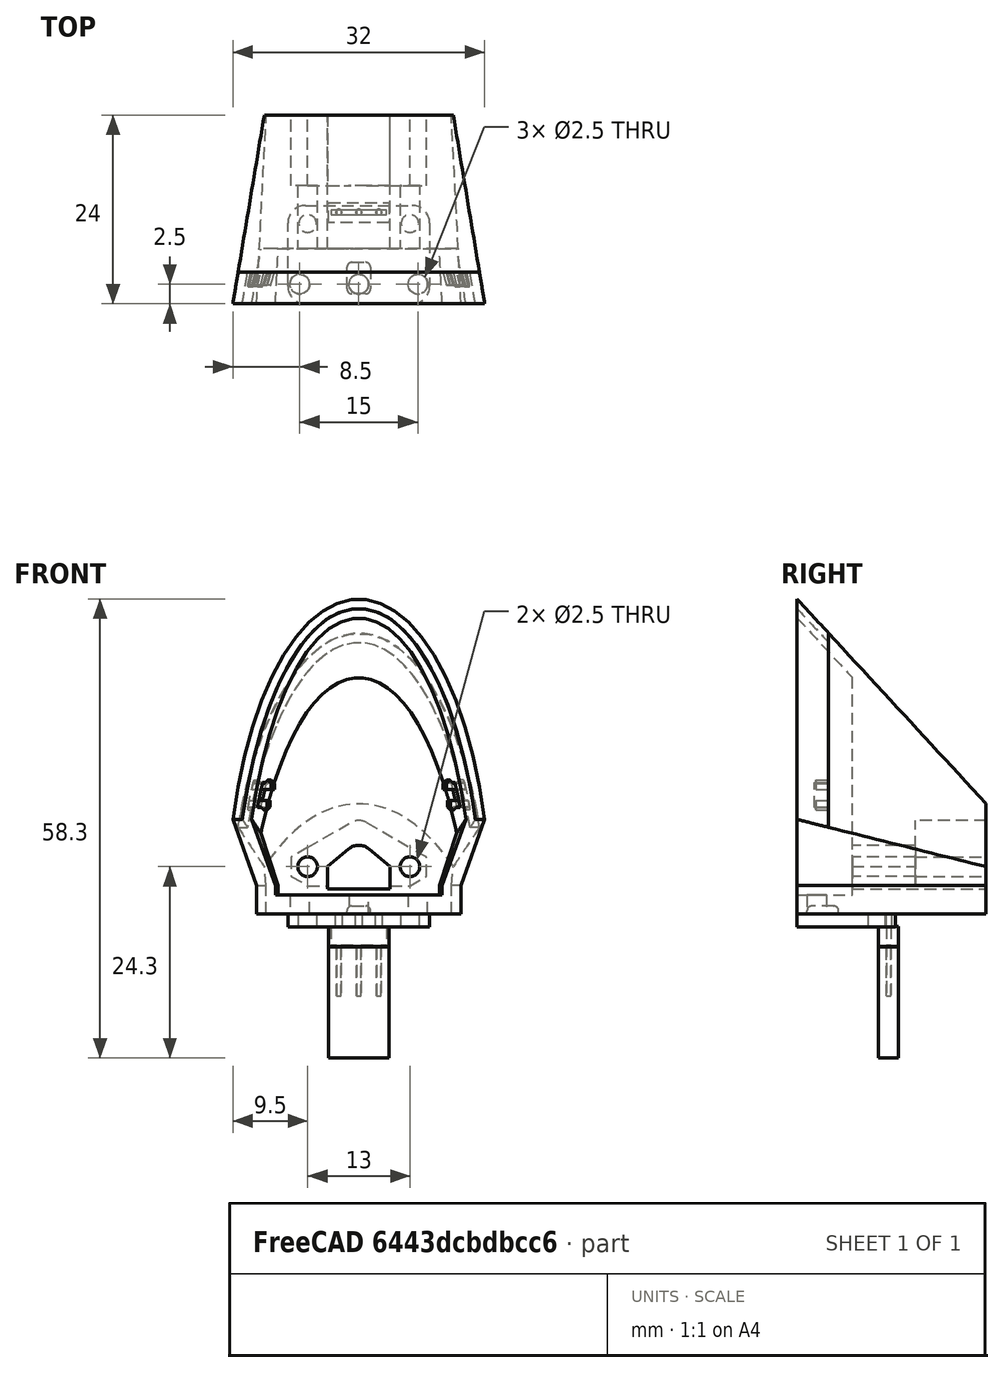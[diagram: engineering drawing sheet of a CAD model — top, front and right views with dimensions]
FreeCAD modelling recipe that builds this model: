
FCSTD DOCUMENT  (FreeCAD 0.19R24276 (Git))
Label: Spec_PB3D_Ear
License: All rights reserved
LicenseURL: http://en.wikipedia.org/wiki/All_rights_reserved
objects: Sketcher::SketchObject×30, PartDesign::Pocket×8, PartDesign::Pad×7, PartDesign::Body×7, PartDesign::Plane×5, PartDesign::SubtractiveLoft×4, Spreadsheet::Sheet×2, PartDesign::AdditiveLoft×2, App::Part×2, PartDesign::Fillet×1, Mesh::Feature×1
note: 86 computed .brp shape members not serialized (recipe doc carries the construction recipe); baked Part::Feature solids carry a one-line shape summary decoded from their .brp

FEATURE [PartDesign::Plane] DatumPlane  label="Datum_EarBack"
  AttachmentOffset = pos=(0,0,-24) rot=(0,0,1;0rad)
  Length = 61.2949
  MapMode = 5
  Placement = pos=(0,24,5.3e-15) rot=(1,0,0;1.5708rad)
  ResizeMode = 0
  Support = -> [XZ_Plane001]
  Width = 75.0828
  expr: .AttachmentOffset.Base.z = -<<params>>.ear_leng
FEATURE [Spreadsheet::Sheet] Spreadsheet  label="params"
  cells = A1=M2 Bolt Clearances; C1=M2.5 Bolt Clearances; E1=Std Dims; G1=Grove Board Dims; A2=Hole Clear Diam; B2(m2_hole_clear_diam)==2.5mm; C2=Hole Clear Diam; D2(m25_hole_clear_diam)==2.8mm; E2=Std. Chamfer; F2(std_chamf)==1mm; G2=Grove Board Width; H2(grove_board_width)==20mm; A3=Head Clear Diam; B3(m2_head_clear_diam)==4.2mm; C3=Head Clear Diam; D3(m25_head_clear_diam)==5.3mm; E3=Std. Radius; F3(std_rad)==2mm; G3=Grove Board Outer Mt Diam; H3(grove_board_mt_outer_diam)==4mm; A4=Head Min Depth; B4(m2_head_min_depth)==1.6mm; C4=Head Min Depth; D4(m25_head_min_depth)==2.3mm; E4=Std. Clear Tol; F4(std_clear_tol)==0.3mm; A5=Nut Clear Flat; B5(m2_nut_clear_flat)==4.2mm; C5=Nut Clear Flat; D5(m25_nut_clear_flat)==5.2mm; A6=Nut Min Depth; B6(m2_nut_min_depth)==1.75mm; C6=Nut Min Depth; D6(m25_nut_min_depth)==2mm; A8=Ear Dims; A9=Ear Base Thick; B9(ear_base_thick)==2mm; C9=Ear Leng; D9(ear_leng)==24mm; E9=Mic Mt Plane Offset Z; F9(mic_mt_plane_offset_z)==7mm; G9=Mic Pins Width; H9(mic_pins_width)==2.54mm * 3; A10=Ear Vert Height; B10(ear_vert_height)==1.6mm; C10=Ear Ellipse Maj Ax; D10(ear_ellipse_majax)==40mm; E10=Mic Mt Hex Offset; F10(mic_mt_hex_offset)==8mm; G10=Mic Pins Base Offset; H10(mic_pins_base_offset)==mic_mt_base_offset - 1.41mm; E11=Mic Mt Hole Space W; F11(mic_mt_hole_space_width)==13mm; G11=Mic Pins Square Block Dim; H11(mic_pins_square_block_dim)==2.54mm; A12=Ear Fr Base Width; B12(ear_front_base_width)==26mm; C12=Ear Mt Hole Offset; D12(ear_mt_hole_offset)==2.5mm; E12=Mic Mt Hole Base Offset; F12(mic_mt_base_offset)==ear_base_thick + 4mm; A13=Ear Fr Mid Width; B13(ear_front_mid_width)==32mm; C13=Ear Mt Hole Width Space; D13(ear_mt_hole_width)==15mm; A14=Ear Fr Mid Height; B14(ear_front_mid_height)==12mm; A15=Ear Fr Tot Height; B15(ear_front_tot_height)==40mm; C15=Ear Wall Thick; D15(ear_wall_thick)==2.4mm; G15=Ear Trm Leng; H15(ear_trim_leng)==4mm; G16=Ear Trm Thick; H16(ear_trim_thick)==1.2mm; A17=Ear Bk Base Width; B17(ear_back_base_width)==23.5mm; C17=Ear Sl Base Width; D17(ear_slope_base_width)==(ear_front_base_width - ear_back_base_width) / ear_leng; E17=Ear GM Base Width; F17(ear_gm_base_width)==ear_front_base_width - ear_slope_base_width * mic_mt_plane_offset_z; G17=Ear Trm Base Width; H17(ear_trim_base_width)==ear_front_base_width - ear_slope_base_width * ear_trim_leng; A18=Ear Bk Mid Width; B18(ear_back_mid_width)==24mm; C18=Ear Sl Mid Width; D18(ear_slope_mid_width)==(ear_front_mid_width - ear_back_mid_width) / ear_leng; E18=Ear GM Mid Width; F18(ear_gm_mid_width)==ear_front_mid_width - ear_slope_mid_width * mic_mt_plane_offset_z; G18=Ear Trm Mid Width; H18(ear_trim_mid_width)==ear_front_mid_width - ear_slope_mid_width * ear_trim_leng; A19=Ear Bk Mid Height; B19(ear_back_mid_height)==6mm; C19=Ear Sl Mid Height; D19(ear_slope_mid_height)==(ear_front_mid_height - ear_back_mid_height) / ear_leng; E19=Ear GM Mid Height; F19(ear_gm_mid_height)==ear_front_mid_height - ear_slope_mid_height * mic_mt_plane_offset_z; G19=Ear Trm Mid Height; H19(ear_trim_mid_height)==ear_front_mid_height - ear_slope_mid_height * ear_trim_leng; A20=Ear Bk Tot Height; B20(ear_back_tot_height)==14mm; C20=Ear Sl Tot Height; D20(ear_slope_tot_height)==(ear_front_tot_height - ear_back_tot_height) / ear_leng; E20=Ear GM Tot Height; F20(ear_gm_tot_height)==ear_front_tot_height - ear_slope_tot_height * mic_mt_plane_offset_z; G20=Ear Trm Tot Height; H20(ear_trim_tot_height)==ear_front_tot_height - ear_slope_tot_height * ear_trim_leng; G22=Ear Trm Clip Width; H22(ear_trim_clip_width)==1.6mm; G23=Ear Trm Clip Height; H23(ear_trim_clip_height)==3mm; G24=Ear Trm Clip Tol; H24(ear_trim_clip_tol)==0.2mm; G25=Ear Trm Clip Thick; H25(ear_trim_clip_thick)==0.8mm; G26=Ear Trm Clip Wedge Size; H26(ear_trim_clip_wedge_size)==0.4mm; G27=Ear Trm Clip Leng; H27(ear_trim_clip_leng)==ear_wall_thick - ear_trim_thick + ear_trim_clip_tol
FEATURE [Sketcher::SketchObject] Sketch  label="Sketch_EarFront"
  FullyConstrained = true
  MapMode = 5
  Placement = pos=(0,0,0) rot=(1,0,0;1.5708rad)
  Support = -> [XZ_Plane001]
  expr: Constraints[30] = <<params>>.ear_base_thick + <<params>>.ear_vert_height
  expr: Constraints[31] = <<params>>.ear_front_mid_height
  expr: Constraints[32] = <<params>>.ear_front_mid_width
  expr: Constraints[33] = <<params>>.ear_front_base_width
  expr: Constraints[34] = <<params>>.ear_front_tot_height
  expr: Constraints[35] = <<params>>.ear_ellipse_majax
  sketch-geometry (15):
    g0: LineSegment StartX=-13 StartY=0 StartZ=0 EndX=13 EndY=0 EndZ=0
    g1: LineSegment StartX=-13 StartY=0 StartZ=0 EndX=-13 EndY=3.6 EndZ=0
    g2: LineSegment StartX=13 StartY=0 StartZ=0 EndX=13 EndY=3.6 EndZ=0
    g3: LineSegment StartX=-13 StartY=3.6 StartZ=0 EndX=13 EndY=3.6 EndZ=0
    g4: LineSegment StartX=13 StartY=3.6 StartZ=0 EndX=16 EndY=12 EndZ=0
    g5: LineSegment StartX=-13 StartY=3.6 StartZ=0 EndX=-16 EndY=12 EndZ=0
    g6: ArcOfEllipse CenterX=0 CenterY=4e-16 CenterZ=0 NormalX=0 NormalY=0 NormalZ=1 MajorRadius=40 MinorRadius=16.7726 AngleXU=1.5708 StartAngle=5.01708 EndAngle=7.54929
    g7: LineSegment StartX=0 StartY=40 StartZ=0 EndX=0 EndY=-40 EndZ=0
    g8: LineSegment StartX=-16.7726 StartY=4e-16 StartZ=0 EndX=16.7726 EndY=4e-16 EndZ=0
    g9: GeomPoint X=4e-15 Y=36.3137 Z=0
    g10: GeomPoint X=0 Y=-36.3137 Z=0
    g11: LineSegment StartX=-16 StartY=12 StartZ=0 EndX=16 EndY=12 EndZ=0
    g12: LineSegment StartX=-13 StartY=3.6 StartZ=0 EndX=-13 EndY=12 EndZ=0
    g13: LineSegment StartX=13 StartY=3.6 StartZ=0 EndX=13 EndY=12 EndZ=0
    g14: LineSegment StartX=-16 StartY=12 StartZ=0 EndX=16 EndY=12 EndZ=0
  constraints (33):
    c: Horizontal(g0)
    c: Symmetric(g0,g0,g-1)
    c: Coincident(g1,g0)
    c: Vertical(g1)
    c: Coincident(g2,g0)
    c: Vertical(g2)
    c: Coincident(g3,g1)
    c: Coincident(g3,g2)
    c: Horizontal(g3)
    c: Coincident(g4,g2)
    c: Coincident(g5,g1)
    c: InternalAlignment(g7-g10 -> g6) x4
    c: PointOnObject(g6,g-2)
    c: Coincident(g11,g5)
    c: Coincident(g11,g4)
    c: Horizontal(g11)
    c: Coincident(g12,g1)
    c: PointOnObject(g12,g11)
    c: Vertical(g12)
    c: Coincident(g13,g2)
    c: PointOnObject(g13,g11)
    c: Vertical(g13)
    c: PointOnObject(g7,g-2)
    c: Coincident(g14,g6)
    c: Coincident(g14,g6)
    c: Coincident(g6,g5)
    c: Coincident(g6,g4)
    c: DistanceY(g0,g2) = 3.6
    c: DistanceY(g-1,g4) = 12
    c: DistanceX(g5,g4) = 32
    c: DistanceX(g0,g0) = 26
    c: DistanceY(g-1,g7) = 40
    c: DistanceY(g8,g7) = 40
FEATURE [Sketcher::SketchObject] Sketch001  label="Sketch_EarBack"
  FullyConstrained = true
  MapMode = 5
  Placement = pos=(0,24,5.3e-15) rot=(1,0,0;1.5708rad)
  Support = -> [DatumPlane]
  expr: Constraints[33] = <<params>>.ear_back_base_width
  expr: Constraints[32] = <<params>>.ear_back_mid_width
  expr: Constraints[31] = <<params>>.ear_back_mid_height
  expr: Constraints[30] = <<params>>.ear_base_thick + <<params>>.ear_vert_height
  expr: Constraints[34] = <<params>>.ear_back_tot_height
  expr: Constraints[35] = <<params>>.ear_ellipse_majax
  sketch-geometry (15):
    g0: LineSegment StartX=-11.75 StartY=0 StartZ=0 EndX=11.75 EndY=0 EndZ=0
    g1: LineSegment StartX=-11.75 StartY=0 StartZ=0 EndX=-11.75 EndY=3.6 EndZ=0
    g2: LineSegment StartX=11.75 StartY=0 StartZ=0 EndX=11.75 EndY=3.6 EndZ=0
    g3: LineSegment StartX=-11.75 StartY=3.6 StartZ=0 EndX=11.75 EndY=3.6 EndZ=0
    g4: LineSegment StartX=11.75 StartY=3.6 StartZ=0 EndX=12 EndY=6 EndZ=0
    g5: LineSegment StartX=-11.75 StartY=3.6 StartZ=0 EndX=-12 EndY=6 EndZ=0
    g6: ArcOfEllipse CenterX=0 CenterY=-26 CenterZ=0 NormalX=0 NormalY=0 NormalZ=1 MajorRadius=40 MinorRadius=20 AngleXU=1.5708 StartAngle=5.63968 EndAngle=6.92669
    g7: LineSegment StartX=0 StartY=14 StartZ=0 EndX=0 EndY=-66 EndZ=0
    g8: LineSegment StartX=-20 StartY=-26 StartZ=0 EndX=20 EndY=-26 EndZ=0
    g9: GeomPoint X=3.8e-15 Y=8.64102 Z=0
    g10: GeomPoint X=0 Y=-60.641 Z=0
    g11: LineSegment StartX=-12 StartY=6 StartZ=0 EndX=12 EndY=6 EndZ=0
    g12: LineSegment StartX=-11.75 StartY=3.6 StartZ=0 EndX=-11.75 EndY=6 EndZ=0
    g13: LineSegment StartX=11.75 StartY=3.6 StartZ=0 EndX=11.75 EndY=6 EndZ=0
    g14: LineSegment StartX=-12 StartY=6 StartZ=0 EndX=12 EndY=6 EndZ=0
  constraints (33):
    c: Horizontal(g0)
    c: Symmetric(g0,g0,g-1)
    c: Coincident(g1,g0)
    c: Vertical(g1)
    c: Coincident(g2,g0)
    c: Vertical(g2)
    c: Coincident(g3,g1)
    c: Coincident(g3,g2)
    c: Horizontal(g3)
    c: Coincident(g4,g2)
    c: Coincident(g5,g1)
    c: InternalAlignment(g7-g10 -> g6) x4
    c: PointOnObject(g6,g-2)
    c: Coincident(g11,g5)
    c: Coincident(g11,g4)
    c: Horizontal(g11)
    c: Coincident(g12,g1)
    c: PointOnObject(g12,g11)
    c: Vertical(g12)
    c: Coincident(g13,g2)
    c: PointOnObject(g13,g11)
    c: Vertical(g13)
    c: PointOnObject(g7,g-2)
    c: Coincident(g14,g6)
    c: Coincident(g14,g6)
    c: Coincident(g6,g5)
    c: Coincident(g6,g4)
    c: DistanceY(g0,g2) = 3.6
    c: DistanceY(g-1,g4) = 6
    c: DistanceX(g5,g4) = 24
    c: DistanceX(g0,g0) = 23.5
    c: DistanceY(g-1,g7) = 14
    c: DistanceY(g6,g7) = 40
FEATURE [PartDesign::AdditiveLoft] AdditiveLoft  label="AdditiveLoft_MainEar"
  Closed = false
  Placement = pos=(0,0,0) rot=(1,0,0;1.5708rad)
  Profile = -> Sketch
  Ruled = false
  Sections = -> [Sketch001]
FEATURE [Sketcher::SketchObject] Sketch002
  FullyConstrained = true
  MapMode = 5
  Support = -> [XY_Plane001]
  expr: Constraints[7] = <<params>>.ear_mt_hole_width
  expr: Constraints[8] = <<params>>.ear_mt_hole_offset
  expr: Constraints[9] = <<params>>.m2_hole_clear_diam
  sketch-geometry (5):
    g0: LineSegment StartX=-7.5 StartY=2.5 StartZ=0 EndX=7.5 EndY=2.5 EndZ=0
    g1: GeomPoint X=0 Y=2.5 Z=0
    g2: Circle CenterX=0 CenterY=2.5 CenterZ=0 NormalX=0 NormalY=0 NormalZ=1 AngleXU=0 Radius=1.25
    g3: Circle CenterX=7.5 CenterY=2.5 CenterZ=0 NormalX=0 NormalY=0 NormalZ=1 AngleXU=0 Radius=1.25
    g4: Circle CenterX=-7.5 CenterY=2.5 CenterZ=0 NormalX=0 NormalY=0 NormalZ=1 AngleXU=0 Radius=1.25
  constraints (11):
    c: Horizontal(g0)
    c: PointOnObject(g1,g-2)
    c: Symmetric(g0,g0,g1)
    c: Coincident(g2,g1)
    c: Coincident(g3,g0)
    c: Coincident(g4,g0)
    c: Equal(g2,g3)
    c: DistanceX(g4,g3) = 15
    c: DistanceY(g-1,g2) = 2.5
    c: Diameter(g3) = 2.5
    c: Equal(g2,g4)
FEATURE [PartDesign::Pocket] Pocket  label="Pocket_MtHoles"
  BaseFeature = -> AdditiveLoft
  Length = 6
  Length2 = 100
  Placement = pos=(0,0,0) rot=(1,0,0;1.5708rad)
  Profile = -> Sketch002
  Reversed = true
  Type = 0
  expr: Length = <<params>>.ear_base_thick * 3
FEATURE [Sketcher::SketchObject] Sketch003  label="Sketch_EarFr_Temp"
  FullyConstrained = true
  MapMode = 5
  Placement = pos=(0,0,0) rot=(1,0,0;1.5708rad)
  Support = -> [XZ_Plane001]
  expr: Constraints[35] = <<params>>.ear_ellipse_majax
  expr: Constraints[34] = <<params>>.ear_front_tot_height
  expr: Constraints[33] = <<params>>.ear_front_base_width
  expr: Constraints[32] = <<params>>.ear_front_mid_width
  expr: Constraints[31] = <<params>>.ear_front_mid_height
  expr: Constraints[30] = <<params>>.ear_base_thick + <<params>>.ear_vert_height
  sketch-geometry (15):
    g0: LineSegment StartX=-13 StartY=0 StartZ=0 EndX=13 EndY=0 EndZ=0
    g1: LineSegment StartX=-13 StartY=0 StartZ=0 EndX=-13 EndY=3.6 EndZ=0
    g2: LineSegment StartX=13 StartY=0 StartZ=0 EndX=13 EndY=3.6 EndZ=0
    g3: LineSegment StartX=-13 StartY=3.6 StartZ=0 EndX=13 EndY=3.6 EndZ=0
    g4: LineSegment StartX=13 StartY=3.6 StartZ=0 EndX=16 EndY=12 EndZ=0
    g5: LineSegment StartX=-13 StartY=3.6 StartZ=0 EndX=-16 EndY=12 EndZ=0
    g6: ArcOfEllipse CenterX=0 CenterY=-7e-16 CenterZ=0 NormalX=0 NormalY=0 NormalZ=1 MajorRadius=40 MinorRadius=16.7726 AngleXU=1.5708 StartAngle=5.01708 EndAngle=7.54929
    g7: LineSegment StartX=0 StartY=40 StartZ=0 EndX=0 EndY=-40 EndZ=0
    g8: LineSegment StartX=-16.7726 StartY=-7e-16 StartZ=0 EndX=16.7726 EndY=-7e-16 EndZ=0
    g9: GeomPoint X=4e-15 Y=36.3137 Z=0
    g10: GeomPoint X=0 Y=-36.3137 Z=0
    g11: LineSegment StartX=-16 StartY=12 StartZ=0 EndX=16 EndY=12 EndZ=0
    g12: LineSegment StartX=-13 StartY=3.6 StartZ=0 EndX=-13 EndY=12 EndZ=0
    g13: LineSegment StartX=13 StartY=3.6 StartZ=0 EndX=13 EndY=12 EndZ=0
    g14: LineSegment StartX=-16 StartY=12 StartZ=0 EndX=16 EndY=12 EndZ=0
  constraints (33):
    c: Horizontal(g0)
    c: Symmetric(g0,g0,g-1)
    c: Coincident(g1,g0)
    c: Vertical(g1)
    c: Coincident(g2,g0)
    c: Vertical(g2)
    c: Coincident(g3,g1)
    c: Coincident(g3,g2)
    c: Horizontal(g3)
    c: Coincident(g4,g2)
    c: Coincident(g5,g1)
    c: InternalAlignment(g7-g10 -> g6) x4
    c: PointOnObject(g6,g-2)
    c: Coincident(g11,g5)
    c: Coincident(g11,g4)
    c: Horizontal(g11)
    c: Coincident(g12,g1)
    c: PointOnObject(g12,g11)
    c: Vertical(g12)
    c: Coincident(g13,g2)
    c: PointOnObject(g13,g11)
    c: Vertical(g13)
    c: PointOnObject(g7,g-2)
    c: Coincident(g14,g6)
    c: Coincident(g14,g6)
    c: Coincident(g6,g5)
    c: Coincident(g6,g4)
    c: DistanceY(g0,g2) = 3.6
    c: DistanceY(g-1,g4) = 12
    c: DistanceX(g5,g4) = 32
    c: DistanceX(g0,g0) = 26
    c: DistanceY(g-1,g7) = 40
    c: DistanceY(g8,g7) = 40
FEATURE [Sketcher::SketchObject] Sketch004  label="Sketch_EarBk_Temp"
  FullyConstrained = true
  MapMode = 5
  Placement = pos=(0,24,5.3e-15) rot=(1,0,0;1.5708rad)
  Support = -> [DatumPlane]
  expr: Constraints[35] = <<params>>.ear_ellipse_majax
  expr: Constraints[34] = <<params>>.ear_back_tot_height
  expr: Constraints[30] = <<params>>.ear_base_thick + <<params>>.ear_vert_height
  expr: Constraints[31] = <<params>>.ear_back_mid_height
  expr: Constraints[32] = <<params>>.ear_back_mid_width
  expr: Constraints[33] = <<params>>.ear_back_base_width
  sketch-geometry (15):
    g0: LineSegment StartX=-11.75 StartY=0 StartZ=0 EndX=11.75 EndY=0 EndZ=0
    g1: LineSegment StartX=-11.75 StartY=0 StartZ=0 EndX=-11.75 EndY=3.6 EndZ=0
    g2: LineSegment StartX=11.75 StartY=0 StartZ=0 EndX=11.75 EndY=3.6 EndZ=0
    g3: LineSegment StartX=-11.75 StartY=3.6 StartZ=0 EndX=11.75 EndY=3.6 EndZ=0
    g4: LineSegment StartX=11.75 StartY=3.6 StartZ=0 EndX=12 EndY=6 EndZ=0
    g5: LineSegment StartX=-11.75 StartY=3.6 StartZ=0 EndX=-12 EndY=6 EndZ=0
    g6: ArcOfEllipse CenterX=0 CenterY=-26 CenterZ=0 NormalX=0 NormalY=0 NormalZ=1 MajorRadius=40 MinorRadius=20 AngleXU=1.5708 StartAngle=5.63968 EndAngle=6.92669
    g7: LineSegment StartX=0 StartY=14 StartZ=0 EndX=0 EndY=-66 EndZ=0
    g8: LineSegment StartX=-20 StartY=-26 StartZ=0 EndX=20 EndY=-26 EndZ=0
    g9: GeomPoint X=3.8e-15 Y=8.64102 Z=0
    g10: GeomPoint X=0 Y=-60.641 Z=0
    g11: LineSegment StartX=-12 StartY=6 StartZ=0 EndX=12 EndY=6 EndZ=0
    g12: LineSegment StartX=-11.75 StartY=3.6 StartZ=0 EndX=-11.75 EndY=6 EndZ=0
    g13: LineSegment StartX=11.75 StartY=3.6 StartZ=0 EndX=11.75 EndY=6 EndZ=0
    g14: LineSegment StartX=-12 StartY=6 StartZ=0 EndX=12 EndY=6 EndZ=0
  constraints (33):
    c: Horizontal(g0)
    c: Symmetric(g0,g0,g-1)
    c: Coincident(g1,g0)
    c: Vertical(g1)
    c: Coincident(g2,g0)
    c: Vertical(g2)
    c: Coincident(g3,g1)
    c: Coincident(g3,g2)
    c: Horizontal(g3)
    c: Coincident(g4,g2)
    c: Coincident(g5,g1)
    c: InternalAlignment(g7-g10 -> g6) x4
    c: PointOnObject(g6,g-2)
    c: Coincident(g11,g5)
    c: Coincident(g11,g4)
    c: Horizontal(g11)
    c: Coincident(g12,g1)
    c: PointOnObject(g12,g11)
    c: Vertical(g12)
    c: Coincident(g13,g2)
    c: PointOnObject(g13,g11)
    c: Vertical(g13)
    c: PointOnObject(g7,g-2)
    c: Coincident(g14,g6)
    c: Coincident(g14,g6)
    c: Coincident(g6,g5)
    c: Coincident(g6,g4)
    c: DistanceY(g0,g2) = 3.6
    c: DistanceY(g-1,g4) = 6
    c: DistanceX(g5,g4) = 24
    c: DistanceX(g0,g0) = 23.5
    c: DistanceY(g-1,g7) = 14
    c: DistanceY(g6,g7) = 40
FEATURE [PartDesign::Plane] DatumPlane001  label="Datum_MicMtPlane"
  AttachmentOffset = pos=(0,0,-7) rot=(0,0,1;0rad)
  Length = 61.2949
  MapMode = 5
  Placement = pos=(0,7,1.6e-15) rot=(1,0,0;1.5708rad)
  ResizeMode = 0
  Support = -> [XZ_Plane001]
  Width = 75.0828
  expr: .AttachmentOffset.Base.z = -<<params>>.mic_mt_plane_offset_z
FEATURE [Sketcher::SketchObject] Sketch015  label="Sketch_GrovePCut"
  FullyConstrained = true
  MapMode = 5
  Placement = pos=(0,7,1.6e-15) rot=(1,0,0;1.5708rad)
  Support = -> [DatumPlane001]
  expr: Constraints[30] = <<params>>.grove_board_width + <<params>>.std_clear_tol
  expr: Constraints[32] = <<params>>.grove_board_mt_outer_diam + <<params>>.std_clear_tol
  expr: Constraints[29] = <<params>>.grove_board_width + <<params>>.std_clear_tol
  expr: Constraints[4] = <<params>>.ear_base_thick - <<params>>.std_clear_tol / 2
  sketch-geometry (12):
    g0: LineSegment StartX=-10.15 StartY=22.15 StartZ=0 EndX=10.15 EndY=22.15 EndZ=0
    g1: LineSegment StartX=10.15 StartY=1.85 StartZ=0 EndX=-10.15 EndY=1.85 EndZ=0
    g2: GeomPoint X=0 Y=1.85 Z=0
    g3: LineSegment StartX=-10.15 StartY=22.15 StartZ=0 EndX=-10.15 EndY=14.15 EndZ=0
    g4: LineSegment StartX=-10.15 StartY=1.85 StartZ=0 EndX=-10.15 EndY=9.85 EndZ=0
    g5: LineSegment StartX=10.15 StartY=1.85 StartZ=0 EndX=10.15 EndY=9.85 EndZ=0
    g6: LineSegment StartX=10.15 StartY=22.15 StartZ=0 EndX=10.15 EndY=14.15 EndZ=0
    g7: ArcOfCircle CenterX=-10.15 CenterY=12 CenterZ=0 NormalX=0 NormalY=0 NormalZ=1 AngleXU=0 Radius=2.15 StartAngle=1.5708 EndAngle=4.71239
    g8: ArcOfCircle CenterX=10.15 CenterY=12 CenterZ=0 NormalX=0 NormalY=0 NormalZ=1 AngleXU=0 Radius=2.15 StartAngle=4.71239 EndAngle=7.85398
    g9: LineSegment StartX=-10.15 StartY=14.15 StartZ=0 EndX=-10.15 EndY=9.85 EndZ=0
    g10: LineSegment StartX=10.15 StartY=14.15 StartZ=0 EndX=10.15 EndY=9.85 EndZ=0
    g11: LineSegment StartX=-10.15 StartY=12 StartZ=0 EndX=10.15 EndY=12 EndZ=0
  constraints (33):
    c: Horizontal(g0)
    c: Horizontal(g1)
    c: PointOnObject(g2,g-2)
    c: Symmetric(g1,g1,g2)
    c: DistanceY(g-1,g2) = 1.85
    c: Coincident(g3,g0)
    c: Vertical(g3)
    c: Coincident(g4,g1)
    c: Vertical(g4)
    c: Coincident(g5,g1)
    c: Vertical(g5)
    c: Coincident(g6,g0)
    c: Vertical(g6)
    c: Coincident(g7,g3)
    c: Coincident(g7,g4)
    c: Coincident(g8,g6)
    c: Coincident(g8,g5)
    c: Coincident(g9,g3)
    c: Coincident(g9,g4)
    c: Vertical(g9)
    c: Coincident(g10,g6)
    c: Coincident(g10,g5)
    c: Vertical(g10)
    c: PointOnObject(g7,g9)
    c: PointOnObject(g8,g10)
    c: Coincident(g11,g7)
    c: Coincident(g11,g8)
    c: Horizontal(g11)
    c: Equal(g6,g5)
    c: DistanceY(g1,g0) = 20.3
    c: DistanceX(g0,g0) = 20.3
    c: Equal(g8,g7)
    c: Diameter(g8) = 4.3
FEATURE [Sketcher::SketchObject] Sketch016  label="Sketch_EarFront_Cut"
  FullyConstrained = true
  MapMode = 5
  Placement = pos=(0,0,0) rot=(1,0,0;1.5708rad)
  Support = -> [XZ_Plane001]
  expr: Constraints[61] = <<params>>.ear_ellipse_majax
  expr: Constraints[52] = <<params>>.ear_wall_thick
  expr: Constraints[60] = <<params>>.ear_wall_thick
  expr: Constraints[35] = <<params>>.ear_ellipse_majax
  expr: Constraints[50] = Spreadsheet.ear_wall_thick
  expr: Constraints[34] = <<params>>.ear_front_tot_height
  expr: Constraints[49] = Spreadsheet.ear_wall_thick
  expr: Constraints[33] = <<params>>.ear_front_base_width
  expr: Constraints[32] = <<params>>.ear_front_mid_width
  expr: Constraints[51] = <<params>>.ear_wall_thick
  expr: Constraints[31] = <<params>>.ear_front_mid_height
  expr: Constraints[30] = <<params>>.ear_base_thick + <<params>>.ear_vert_height
  sketch-geometry (26):
    g0: LineSegment StartX=-13 StartY=0 StartZ=0 EndX=13 EndY=0 EndZ=0
    g1: LineSegment StartX=-13 StartY=0 StartZ=0 EndX=-13 EndY=3.6 EndZ=0
    g2: LineSegment StartX=13 StartY=0 StartZ=0 EndX=13 EndY=3.6 EndZ=0
    g3: LineSegment StartX=-13 StartY=3.6 StartZ=0 EndX=13 EndY=3.6 EndZ=0
    g4: LineSegment StartX=13 StartY=3.6 StartZ=0 EndX=16 EndY=12 EndZ=0
    g5: LineSegment StartX=-13 StartY=3.6 StartZ=0 EndX=-16 EndY=12 EndZ=0
    g6: ArcOfEllipse CenterX=0 CenterY=7e-16 CenterZ=0 NormalX=0 NormalY=0 NormalZ=1 MajorRadius=40 MinorRadius=16.7726 AngleXU=1.5708 StartAngle=5.01708 EndAngle=7.54929
    g7: LineSegment StartX=0 StartY=40 StartZ=0 EndX=0 EndY=-40 EndZ=0
    g8: LineSegment StartX=-16.7726 StartY=7e-16 StartZ=0 EndX=16.7726 EndY=7e-16 EndZ=0
    g9: GeomPoint X=4e-15 Y=36.3137 Z=0
    g10: GeomPoint X=0 Y=-36.3137 Z=0
    g11: LineSegment StartX=-16 StartY=12 StartZ=0 EndX=16 EndY=12 EndZ=0
    g12: LineSegment StartX=-13 StartY=3.6 StartZ=0 EndX=-13 EndY=12 EndZ=0
    g13: LineSegment StartX=13 StartY=3.6 StartZ=0 EndX=13 EndY=12 EndZ=0
    g14: LineSegment StartX=-16 StartY=12 StartZ=0 EndX=16 EndY=12 EndZ=0
    g15: LineSegment StartX=-10.6 StartY=2.4 StartZ=0 EndX=10.6 EndY=2.4 EndZ=0
    g16: GeomPoint X=0 Y=2.4 Z=0
    g17: LineSegment StartX=-10.6 StartY=2.4 StartZ=0 EndX=-10.6 EndY=3.6 EndZ=0
    g18: LineSegment StartX=-10.6 StartY=3.6 StartZ=0 EndX=-13.6 EndY=12 EndZ=0
    g19: LineSegment StartX=10.6 StartY=2.4 StartZ=0 EndX=10.6 EndY=3.6 EndZ=0
    g20: LineSegment StartX=10.6 StartY=3.6 StartZ=0 EndX=13.6 EndY=12 EndZ=0
    g21: ArcOfEllipse CenterX=0 CenterY=-2.4 CenterZ=0 NormalX=0 NormalY=0 NormalZ=1 MajorRadius=40 MinorRadius=14.5774 AngleXU=1.5708 StartAngle=5.08066 EndAngle=7.48571
    g22: LineSegment StartX=-7e-16 StartY=37.6 StartZ=0 EndX=7e-16 EndY=-42.4 EndZ=0
    g23: LineSegment StartX=-14.5774 StartY=-2.4 StartZ=0 EndX=14.5774 EndY=-2.4 EndZ=0
    g24: GeomPoint X=4.1e-15 Y=34.8492 Z=0
    g25: GeomPoint X=6e-16 Y=-39.6492 Z=0
  constraints (56):
    c: Horizontal(g0)
    c: Symmetric(g0,g0,g-1)
    c: Coincident(g1,g0)
    c: Vertical(g1)
    c: Coincident(g2,g0)
    c: Vertical(g2)
    c: Coincident(g3,g1)
    c: Coincident(g3,g2)
    c: Horizontal(g3)
    c: Coincident(g4,g2)
    c: Coincident(g5,g1)
    c: InternalAlignment(g7-g10 -> g6) x4
    c: PointOnObject(g6,g-2)
    c: Coincident(g11,g5)
    c: Coincident(g11,g4)
    c: Horizontal(g11)
    c: Coincident(g12,g1)
    c: PointOnObject(g12,g11)
    c: Vertical(g12)
    c: Coincident(g13,g2)
    c: PointOnObject(g13,g11)
    c: Vertical(g13)
    c: PointOnObject(g7,g-2)
    c: Coincident(g14,g6)
    c: Coincident(g14,g6)
    c: Coincident(g6,g5)
    c: Coincident(g6,g4)
    c: DistanceY(g0,g2) = 3.6
    c: DistanceY(g-1,g4) = 12
    c: DistanceX(g5,g4) = 32
    c: DistanceX(g0,g0) = 26
    c: DistanceY(g-1,g7) = 40
    c: DistanceY(g8,g7) = 40
    c: Horizontal(g15)
    c: PointOnObject(g16,g7)
    c: Symmetric(g15,g15,g16)
    c: Coincident(g17,g15)
    c: PointOnObject(g17,g3)
    c: Vertical(g17)
    c: Coincident(g18,g17)
    c: PointOnObject(g18,g11)
    c: Coincident(g19,g15)
    c: PointOnObject(g19,g3)
    c: Vertical(g19)
    c: Coincident(g20,g19)
    c: PointOnObject(g20,g11)
    c: DistanceX(g19,g2) = 2.4
    c: DistanceY(g-1,g16) = 2.4
    c: DistanceX(g20,g4) = 2.4
    c: DistanceX(g5,g18) = 2.4
    c: InternalAlignment(g22-g25 -> g21) x4
    c: PointOnObject(g21,g7)
    c: Coincident(g21,g18)
    c: Coincident(g21,g20)
    c: DistanceY(g22,g7) = 2.4
    c: DistanceY(g21,g22) = 40
FEATURE [Sketcher::SketchObject] Sketch017  label="Sketch_EarMicMt_Cut"
  FullyConstrained = true
  MapMode = 5
  Placement = pos=(0,7,1.6e-15) rot=(1,0,0;1.5708rad)
  Support = -> [DatumPlane001]
  expr: Constraints[30] = <<params>>.ear_base_thick + <<params>>.ear_vert_height
  expr: Constraints[31] = <<params>>.ear_gm_mid_height
  expr: Constraints[51] = <<params>>.ear_wall_thick
  expr: Constraints[32] = <<params>>.ear_gm_mid_width
  expr: Constraints[33] = <<params>>.ear_gm_base_width
  expr: Constraints[49] = Spreadsheet.ear_wall_thick
  expr: Constraints[34] = <<params>>.ear_gm_tot_height
  expr: Constraints[50] = Spreadsheet.ear_wall_thick
  expr: Constraints[35] = <<params>>.ear_ellipse_majax
  expr: Constraints[60] = <<params>>.ear_wall_thick
  expr: Constraints[52] = <<params>>.ear_wall_thick
  expr: Constraints[61] = <<params>>.ear_ellipse_majax
  sketch-geometry (26):
    g0: LineSegment StartX=-12.6354 StartY=0 StartZ=0 EndX=12.6354 EndY=0 EndZ=0
    g1: LineSegment StartX=-12.6354 StartY=0 StartZ=0 EndX=-12.6354 EndY=3.6 EndZ=0
    g2: LineSegment StartX=12.6354 StartY=0 StartZ=0 EndX=12.6354 EndY=3.6 EndZ=0
    g3: LineSegment StartX=-12.6354 StartY=3.6 StartZ=0 EndX=12.6354 EndY=3.6 EndZ=0
    g4: LineSegment StartX=12.6354 StartY=3.6 StartZ=0 EndX=14.8333 EndY=10.25 EndZ=0
    g5: LineSegment StartX=-12.6354 StartY=3.6 StartZ=0 EndX=-14.8333 EndY=10.25 EndZ=0
    g6: ArcOfEllipse CenterX=0 CenterY=-7.58333 CenterZ=0 NormalX=0 NormalY=0 NormalZ=1 MajorRadius=40 MinorRadius=16.5714 AngleXU=1.5708 StartAngle=5.17449 EndAngle=7.39188
    g7: LineSegment StartX=0 StartY=32.4167 StartZ=0 EndX=0 EndY=-47.5833 EndZ=0
    g8: LineSegment StartX=-16.5714 StartY=-7.58333 StartZ=0 EndX=16.5714 EndY=-7.58333 EndZ=0
    g9: GeomPoint X=4e-15 Y=28.8226 Z=0
    g10: GeomPoint X=0 Y=-43.9892 Z=0
    g11: LineSegment StartX=-14.8333 StartY=10.25 StartZ=0 EndX=14.8333 EndY=10.25 EndZ=0
    g12: LineSegment StartX=-12.6354 StartY=3.6 StartZ=0 EndX=-12.6354 EndY=10.25 EndZ=0
    g13: LineSegment StartX=12.6354 StartY=3.6 StartZ=0 EndX=12.6354 EndY=10.25 EndZ=0
    g14: LineSegment StartX=-14.8333 StartY=10.25 StartZ=0 EndX=14.8333 EndY=10.25 EndZ=0
    g15: LineSegment StartX=-10.2354 StartY=2.4 StartZ=0 EndX=10.2354 EndY=2.4 EndZ=0
    g16: GeomPoint X=0 Y=2.4 Z=0
    g17: LineSegment StartX=-10.2354 StartY=2.4 StartZ=0 EndX=-10.2354 EndY=3.6 EndZ=0
    g18: LineSegment StartX=-10.2354 StartY=3.6 StartZ=0 EndX=-12.4333 EndY=10.25 EndZ=0
    g19: LineSegment StartX=10.2354 StartY=2.4 StartZ=0 EndX=10.2354 EndY=3.6 EndZ=0
    g20: LineSegment StartX=10.2354 StartY=3.6 StartZ=0 EndX=12.4333 EndY=10.25 EndZ=0
    g21: ArcOfEllipse CenterX=0 CenterY=-9.98333 CenterZ=0 NormalX=0 NormalY=0 NormalZ=1 MajorRadius=40 MinorRadius=14.4133 AngleXU=1.5708 StartAngle=5.24274 EndAngle=7.32363
    g22: LineSegment StartX=-2.9e-15 StartY=30.0167 StartZ=0 EndX=2.9e-15 EndY=-49.9833 EndZ=0
    g23: LineSegment StartX=-14.4133 StartY=-9.98333 StartZ=0 EndX=14.4133 EndY=-9.98333 EndZ=0
    g24: GeomPoint X=-8.3e-15 Y=27.3296 Z=0
    g25: GeomPoint X=2.8e-15 Y=-47.2963 Z=0
  constraints (56):
    c: Horizontal(g0)
    c: Symmetric(g0,g0,g-1)
    c: Coincident(g1,g0)
    c: Vertical(g1)
    c: Coincident(g2,g0)
    c: Vertical(g2)
    c: Coincident(g3,g1)
    c: Coincident(g3,g2)
    c: Horizontal(g3)
    c: Coincident(g4,g2)
    c: Coincident(g5,g1)
    c: InternalAlignment(g7-g10 -> g6) x4
    c: PointOnObject(g6,g-2)
    c: Coincident(g11,g5)
    c: Coincident(g11,g4)
    c: Horizontal(g11)
    c: Coincident(g12,g1)
    c: PointOnObject(g12,g11)
    c: Vertical(g12)
    c: Coincident(g13,g2)
    c: PointOnObject(g13,g11)
    c: Vertical(g13)
    c: PointOnObject(g7,g-2)
    c: Coincident(g14,g6)
    c: Coincident(g14,g6)
    c: Coincident(g6,g5)
    c: Coincident(g6,g4)
    c: DistanceY(g0,g2) = 3.6
    c: DistanceY(g-1,g4) = 10.25
    c: DistanceX(g5,g4) = 29.6667
    c: DistanceX(g0,g0) = 25.2708
    c: DistanceY(g-1,g7) = 32.4167
    c: DistanceY(g8,g7) = 40
    c: Horizontal(g15)
    c: PointOnObject(g16,g7)
    c: Symmetric(g15,g15,g16)
    c: Coincident(g17,g15)
    c: PointOnObject(g17,g3)
    c: Vertical(g17)
    c: Coincident(g18,g17)
    c: PointOnObject(g18,g11)
    c: Coincident(g19,g15)
    c: PointOnObject(g19,g3)
    c: Vertical(g19)
    c: Coincident(g20,g19)
    c: PointOnObject(g20,g11)
    c: DistanceX(g19,g2) = 2.4
    c: DistanceY(g-1,g16) = 2.4
    c: DistanceX(g20,g4) = 2.4
    c: DistanceX(g5,g18) = 2.4
    c: InternalAlignment(g22-g25 -> g21) x4
    c: PointOnObject(g21,g7)
    c: Coincident(g21,g18)
    c: Coincident(g21,g20)
    c: DistanceY(g22,g7) = 2.4
    c: DistanceY(g21,g22) = 40
FEATURE [PartDesign::SubtractiveLoft] SubtractiveLoft
  BaseFeature = -> Pocket
  Closed = false
  Placement = pos=(0,0,0) rot=(1,0,0;1.5708rad)
  Profile = -> Sketch016
  Ruled = false
  Sections = -> [Sketch017]
FEATURE [Sketcher::SketchObject] Sketch018
  FullyConstrained = true
  MapMode = 5
  Placement = pos=(0,7,1.6e-15) rot=(1,0,0;1.5708rad)
  Support = -> [DatumPlane001]
  expr: Constraints[8] = <<params>>.mic_mt_base_offset
  expr: Constraints[7] = <<params>>.m2_hole_clear_diam
  expr: Constraints[3] = <<params>>.mic_mt_hole_space_width
  sketch-geometry (4):
    g0: LineSegment StartX=-6.5 StartY=6 StartZ=0 EndX=6.5 EndY=6 EndZ=0
    g1: GeomPoint X=0 Y=6 Z=0
    g2: Circle CenterX=-6.5 CenterY=6 CenterZ=0 NormalX=0 NormalY=0 NormalZ=1 AngleXU=0 Radius=1.25
    g3: Circle CenterX=6.5 CenterY=6 CenterZ=0 NormalX=0 NormalY=0 NormalZ=1 AngleXU=0 Radius=1.25
  constraints (9):
    c: Horizontal(g0)
    c: PointOnObject(g1,g-2)
    c: Symmetric(g0,g0,g1)
    c: DistanceX(g0,g0) = 13
    c: Coincident(g2,g0)
    c: Coincident(g3,g0)
    c: Equal(g3,g2)
    c: Diameter(g3) = 2.5
    c: DistanceY(g-1,g1) = 6
FEATURE [PartDesign::Pocket] Pocket008  label="Pocket_MicMtHoles"
  BaseFeature = -> SubtractiveLoft
  Length = 5
  Length2 = 100
  Placement = pos=(0,0,0) rot=(1,0,0;1.5708rad)
  Profile = -> Sketch018
  Type = 1
FEATURE [PartDesign::Plane] DatumPlane002  label="Datum_MicHexOffset"
  AttachmentOffset = pos=(0,0,-15) rot=(0,0,1;0rad)
  Length = 61.2949
  MapMode = 5
  Placement = pos=(0,15,3.3e-15) rot=(1,0,0;1.5708rad)
  ResizeMode = 0
  Support = -> [XZ_Plane001]
  Width = 75.0828
  expr: .AttachmentOffset.Base.z = -1 * (<<params>>.mic_mt_plane_offset_z + <<params>>.mic_mt_hex_offset)
FEATURE [Sketcher::SketchObject] Sketch019
  FullyConstrained = true
  MapMode = 5
  Placement = pos=(0,15,3.3e-15) rot=(1,0,0;1.5708rad)
  Support = -> [DatumPlane002]
  expr: Constraints[52] = <<params>>.std_rad
  expr: Constraints[44] = <<params>>.mic_mt_base_offset
  expr: Constraints[43] = <<params>>.m2_nut_clear_flat
  expr: Constraints[3] = <<params>>.mic_mt_hole_space_width
  sketch-geometry (20):
    g0: LineSegment StartX=-6.5 StartY=6 StartZ=0 EndX=6.5 EndY=6 EndZ=0
    g1: GeomPoint X=0 Y=6 Z=0
    g2: LineSegment StartX=-6.5 StartY=8.42487 StartZ=0 EndX=-8.6 EndY=7.21244 EndZ=0
    g3: LineSegment StartX=-8.6 StartY=7.21244 StartZ=0 EndX=-8.6 EndY=4.78756 EndZ=0
    g4: LineSegment StartX=-8.6 StartY=4.78756 StartZ=0 EndX=-6.5 EndY=3.57513 EndZ=0
    g5: LineSegment StartX=-6.5 StartY=3.57513 StartZ=0 EndX=-4.4 EndY=4.78756 EndZ=0
    g6: LineSegment StartX=-4.4 StartY=4.78756 StartZ=0 EndX=-4.4 EndY=7.21244 EndZ=0
    g7: LineSegment StartX=-4.4 StartY=7.21244 StartZ=0 EndX=-6.5 EndY=8.42487 EndZ=0
    g8: Circle CenterX=-6.5 CenterY=6 CenterZ=0 NormalX=0 NormalY=0 NormalZ=1 AngleXU=0 Radius=2.42487
    g9: LineSegment StartX=6.5 StartY=8.42487 StartZ=0 EndX=4.4 EndY=7.21244 EndZ=0
    g10: LineSegment StartX=4.4 StartY=7.21244 StartZ=0 EndX=4.4 EndY=4.78756 EndZ=0
    g11: LineSegment StartX=4.4 StartY=4.78756 StartZ=0 EndX=6.5 EndY=3.57513 EndZ=0
    g12: LineSegment StartX=6.5 StartY=3.57513 StartZ=0 EndX=8.6 EndY=4.78756 EndZ=0
    g13: LineSegment StartX=8.6 StartY=4.78756 StartZ=0 EndX=8.6 EndY=7.21244 EndZ=0
    g14: LineSegment StartX=8.6 StartY=7.21244 StartZ=0 EndX=6.5 EndY=8.42487 EndZ=0
    g15: Circle CenterX=6.5 CenterY=6 CenterZ=0 NormalX=0 NormalY=0 NormalZ=1 AngleXU=0 Radius=2.42487
    g16: LineSegment StartX=-6.5 StartY=8.42487 StartZ=0 EndX=-1 EndY=11.6003 EndZ=0
    g17: LineSegment StartX=1 StartY=11.6003 StartZ=0 EndX=6.5 EndY=8.42487 EndZ=0
    g18: LineSegment StartX=-6.5 StartY=3.57513 StartZ=0 EndX=6.5 EndY=3.57513 EndZ=0
    g19: ArcOfCircle CenterX=0 CenterY=9.86825 CenterZ=0 NormalX=0 NormalY=0 NormalZ=1 AngleXU=0 Radius=2 StartAngle=1.0472 EndAngle=2.0944
  constraints (46):
    c: Horizontal(g0)
    c: PointOnObject(g1,g-2)
    c: Symmetric(g0,g0,g1)
    c: DistanceX(g0,g0) = 13
    c: Coincident(g2,g3)
    c: Coincident(g3,g4)
    c: Coincident(g4,g5)
    c: Coincident(g5,g6)
    c: Coincident(g6,g7)
    c: Coincident(g7,g2)
    c: Equal(g2, g3-g7) x5
    c: PointOnObject(g2,g8)
    c: PointOnObject(g3,g8)
    c: PointOnObject(g4,g8)
    c: PointOnObject(g5,g8)
    c: PointOnObject(g6,g8)
    c: PointOnObject(g7,g8)
    c: Coincident(g8,g0)
    c: Coincident(g9,g10)
    c: Coincident(g10,g11)
    c: Coincident(g11,g12)
    c: Coincident(g12,g13)
    c: Coincident(g13,g14)
    c: Coincident(g14,g9)
    c: Equal(g9, g10-g14) x5
    c: PointOnObject(g9,g15)
    c: PointOnObject(g10,g15)
    c: PointOnObject(g11,g15)
    c: PointOnObject(g12,g15)
    c: PointOnObject(g13,g15)
    c: PointOnObject(g14,g15)
    c: Coincident(g15,g0)
    c: Equal(g8,g15)
    c: Vertical(g6)
    c: Vertical(g10)
    c: DistanceX(g9,g13) = 4.2
    c: DistanceY(g-1,g1) = 6
    c: Coincident(g16,g2)
    c: Coincident(g17,g9)
    c: Coincident(g18,g4)
    c: Coincident(g18,g11)
    c: Tangent(g16,g19) = 1.5708
    c: Tangent(g17,g19) = 1.5708
    c: PointOnObject(g19,g-2)
    c: Radius(g19) = 2
    c: Parallel(g16,g2)
FEATURE [PartDesign::Pocket] Pocket009  label="Pocket_MicHexSunk"
  BaseFeature = -> Pocket008
  Length = 5
  Length2 = 100
  Placement = pos=(0,0,0) rot=(1,0,0;1.5708rad)
  Profile = -> Sketch019
  Type = 1
FEATURE [Sketcher::SketchObject] Sketch020  label="Sketch_EarTrimFr"
  FullyConstrained = true
  MapMode = 5
  Placement = pos=(0,0,0) rot=(1,0,0;1.5708rad)
  Support = -> [XZ_Plane009]
  expr: Constraints[30] = <<params>>.ear_base_thick + <<params>>.ear_vert_height
  expr: Constraints[31] = <<params>>.ear_front_mid_height
  expr: Constraints[32] = <<params>>.ear_front_mid_width
  expr: Constraints[33] = <<params>>.ear_front_base_width
  expr: Constraints[45] = <<params>>.ear_trim_thick
  expr: Constraints[34] = <<params>>.ear_front_tot_height
  expr: Constraints[35] = <<params>>.ear_ellipse_majax
  expr: Constraints[40] = <<params>>.ear_ellipse_majax
  expr: Constraints[46] = <<params>>.ear_trim_thick
  expr: Constraints[55] = <<params>>.ear_ellipse_majax
  sketch-geometry (27):
    g0: LineSegment StartX=-13 StartY=0 StartZ=0 EndX=13 EndY=0 EndZ=0
    g1: LineSegment StartX=-13 StartY=0 StartZ=0 EndX=-13 EndY=3.6 EndZ=0
    g2: LineSegment StartX=13 StartY=0 StartZ=0 EndX=13 EndY=3.6 EndZ=0
    g3: LineSegment StartX=-13 StartY=3.6 StartZ=0 EndX=13 EndY=3.6 EndZ=0
    g4: LineSegment StartX=13 StartY=3.6 StartZ=0 EndX=16 EndY=12 EndZ=0
    g5: LineSegment StartX=-13 StartY=3.6 StartZ=0 EndX=-16 EndY=12 EndZ=0
    g6: ArcOfEllipse CenterX=0 CenterY=-1.9e-15 CenterZ=0 NormalX=0 NormalY=0 NormalZ=1 MajorRadius=40 MinorRadius=16.7726 AngleXU=1.5708 StartAngle=5.01708 EndAngle=7.54929
    g7: LineSegment StartX=0 StartY=40 StartZ=0 EndX=0 EndY=-40 EndZ=0
    g8: LineSegment StartX=-16.7726 StartY=-1.9e-15 StartZ=0 EndX=16.7726 EndY=-1.9e-15 EndZ=0
    g9: GeomPoint X=4e-15 Y=36.3137 Z=0
    g10: GeomPoint X=0 Y=-36.3137 Z=0
    g11: LineSegment StartX=-16 StartY=12 StartZ=0 EndX=16 EndY=12 EndZ=0
    g12: LineSegment StartX=-13 StartY=3.6 StartZ=0 EndX=-13 EndY=12 EndZ=0
    g13: LineSegment StartX=13 StartY=3.6 StartZ=0 EndX=13 EndY=12 EndZ=0
    g14: LineSegment StartX=-16 StartY=12 StartZ=0 EndX=16 EndY=12 EndZ=0
    g15: ArcOfEllipse CenterX=0 CenterY=-1.2 CenterZ=0 NormalX=0 NormalY=0 NormalZ=1 MajorRadius=40 MinorRadius=15.6783 AngleXU=1.5708 StartAngle=5.04869 EndAngle=7.51768
    g16: LineSegment StartX=0 StartY=38.8 StartZ=0 EndX=0 EndY=-41.2 EndZ=0
    g17: LineSegment StartX=-15.6783 StartY=-1.2 StartZ=0 EndX=15.6783 EndY=-1.2 EndZ=0
    g18: GeomPoint X=4.1e-15 Y=35.5993 Z=0
    g19: GeomPoint X=0 Y=-37.9993 Z=0
    g20: LineSegment StartX=-14.8 StartY=12 StartZ=0 EndX=-16 EndY=12 EndZ=0
    g21: LineSegment StartX=14.8 StartY=12 StartZ=0 EndX=16 EndY=12 EndZ=0
    g22: ArcOfEllipse CenterX=3e-16 CenterY=-3e-16 CenterZ=0 NormalX=0 NormalY=0 NormalZ=1 MajorRadius=40 MinorRadius=16.7726 AngleXU=1.5708 StartAngle=5.01708 EndAngle=7.54929
    g23: LineSegment StartX=0 StartY=40 StartZ=0 EndX=6e-16 EndY=-40 EndZ=0
    g24: LineSegment StartX=-16.7726 StartY=-4e-16 StartZ=0 EndX=16.7726 EndY=-2e-16 EndZ=0
    g25: GeomPoint X=4.3e-15 Y=36.3137 Z=0
    g26: GeomPoint X=6e-16 Y=-36.3137 Z=0
  constraints (50):
    c: Horizontal(g0)
    c: Symmetric(g0,g0,g-1)
    c: Coincident(g1,g0)
    c: Vertical(g1)
    c: Coincident(g2,g0)
    c: Vertical(g2)
    c: Coincident(g3,g1)
    c: Coincident(g3,g2)
    c: Horizontal(g3)
    c: Coincident(g4,g2)
    c: Coincident(g5,g1)
    c: InternalAlignment(g7-g10 -> g6) x4
    c: PointOnObject(g6,g-2)
    c: Coincident(g11,g5)
    c: Coincident(g11,g4)
    c: Horizontal(g11)
    c: Coincident(g12,g1)
    c: PointOnObject(g12,g11)
    c: Vertical(g12)
    c: Coincident(g13,g2)
    c: PointOnObject(g13,g11)
    c: Vertical(g13)
    c: PointOnObject(g7,g-2)
    c: Coincident(g14,g6)
    c: Coincident(g14,g6)
    c: Coincident(g6,g5)
    c: Coincident(g6,g4)
    c: DistanceY(g0,g2) = 3.6
    c: DistanceY(g-1,g4) = 12
    c: DistanceX(g5,g4) = 32
    c: DistanceX(g0,g0) = 26
    c: DistanceY(g-1,g7) = 40
    c: DistanceY(g8,g7) = 40
    c: InternalAlignment(g16-g19 -> g15) x4
    c: DistanceY(g17,g16) = 40
    c: Vertical(g16)
    c: PointOnObject(g16,g-2)
    c: PointOnObject(g15,g11)
    c: PointOnObject(g15,g11)
    c: DistanceX(g15,g4) = 1.2
    c: DistanceY(g16,g7) = 1.2
    c: Coincident(g20,g15)
    c: Coincident(g20,g5)
    c: Coincident(g21,g15)
    c: Coincident(g21,g4)
    c: InternalAlignment(g23-g26 -> g22) x4
    c: DistanceY(g22,g23) = 40
    c: Coincident(g22,g20)
    c: Coincident(g22,g21)
    c: Coincident(g23,g7)
FEATURE [PartDesign::Plane] DatumPlane003  label="Datum_EarTrimBack"
  AttachmentOffset = pos=(0,0,-4) rot=(0,0,1;0rad)
  Length = 61.3994
  MapMode = 5
  Placement = pos=(0,4,9e-16) rot=(1,0,0;1.5708rad)
  ResizeMode = 0
  Support = -> [XZ_Plane009]
  Width = 76.373
  expr: .AttachmentOffset.Base.z = -1 * <<params>>.ear_trim_leng
FEATURE [Sketcher::SketchObject] Sketch021  label="Sketch_EarTrimBk"
  FullyConstrained = true
  MapMode = 5
  Placement = pos=(0,4,9e-16) rot=(1,0,0;1.5708rad)
  Support = -> [DatumPlane003]
  expr: Constraints[55] = <<params>>.ear_ellipse_majax
  expr: Constraints[46] = <<params>>.ear_trim_thick
  expr: Constraints[40] = <<params>>.ear_ellipse_majax
  expr: Constraints[35] = <<params>>.ear_ellipse_majax
  expr: Constraints[34] = <<params>>.ear_trim_tot_height
  expr: Constraints[45] = <<params>>.ear_trim_thick
  expr: Constraints[33] = <<params>>.ear_trim_base_width
  expr: Constraints[32] = <<params>>.ear_trim_mid_width
  expr: Constraints[31] = <<params>>.ear_trim_mid_height
  expr: Constraints[30] = <<params>>.ear_base_thick + <<params>>.ear_vert_height
  sketch-geometry (27):
    g0: LineSegment StartX=-12.7917 StartY=0 StartZ=0 EndX=12.7917 EndY=0 EndZ=0
    g1: LineSegment StartX=-12.7917 StartY=0 StartZ=0 EndX=-12.7917 EndY=3.6 EndZ=0
    g2: LineSegment StartX=12.7917 StartY=0 StartZ=0 EndX=12.7917 EndY=3.6 EndZ=0
    g3: LineSegment StartX=-12.7917 StartY=3.6 StartZ=0 EndX=12.7917 EndY=3.6 EndZ=0
    g4: LineSegment StartX=12.7917 StartY=3.6 StartZ=0 EndX=15.3333 EndY=11 EndZ=0
    g5: LineSegment StartX=-12.7917 StartY=3.6 StartZ=0 EndX=-15.3333 EndY=11 EndZ=0
    g6: ArcOfEllipse CenterX=0 CenterY=-4.33333 CenterZ=0 NormalX=0 NormalY=0 NormalZ=1 MajorRadius=40 MinorRadius=16.6015 AngleXU=1.5708 StartAngle=5.10579 EndAngle=7.46058
    g7: LineSegment StartX=0 StartY=35.6667 StartZ=0 EndX=0 EndY=-44.3333 EndZ=0
    g8: LineSegment StartX=-16.6015 StartY=-4.33333 StartZ=0 EndX=16.6015 EndY=-4.33333 EndZ=0
    g9: GeomPoint X=4e-15 Y=32.0588 Z=0
    g10: GeomPoint X=0 Y=-40.7255 Z=0
    g11: LineSegment StartX=-15.3333 StartY=11 StartZ=0 EndX=15.3333 EndY=11 EndZ=0
    g12: LineSegment StartX=-12.7917 StartY=3.6 StartZ=0 EndX=-12.7917 EndY=11 EndZ=0
    g13: LineSegment StartX=12.7917 StartY=3.6 StartZ=0 EndX=12.7917 EndY=11 EndZ=0
    g14: LineSegment StartX=-15.3333 StartY=11 StartZ=0 EndX=15.3333 EndY=11 EndZ=0
    g15: ArcOfEllipse CenterX=0 CenterY=-5.53333 CenterZ=0 NormalX=0 NormalY=0 NormalZ=1 MajorRadius=40 MinorRadius=15.5212 AngleXU=1.5708 StartAngle=5.1385 EndAngle=7.42787
    g16: LineSegment StartX=0 StartY=34.4667 StartZ=0 EndX=0 EndY=-45.5333 EndZ=0
    g17: LineSegment StartX=-15.5212 StartY=-5.53333 StartZ=0 EndX=15.5212 EndY=-5.53333 EndZ=0
    g18: GeomPoint X=4.1e-15 Y=31.3325 Z=0
    g19: GeomPoint X=0 Y=-42.3992 Z=0
    g20: LineSegment StartX=-14.1333 StartY=11 StartZ=0 EndX=-15.3333 EndY=11 EndZ=0
    g21: LineSegment StartX=14.1333 StartY=11 StartZ=0 EndX=15.3333 EndY=11 EndZ=0
    g22: ArcOfEllipse CenterX=0 CenterY=-4.33333 CenterZ=0 NormalX=0 NormalY=0 NormalZ=1 MajorRadius=40 MinorRadius=16.6015 AngleXU=1.5708 StartAngle=5.10579 EndAngle=7.46058
    g23: LineSegment StartX=0 StartY=35.6667 StartZ=0 EndX=-1e-16 EndY=-44.3333 EndZ=0
    g24: LineSegment StartX=-16.6015 StartY=-4.33333 StartZ=0 EndX=16.6015 EndY=-4.33333 EndZ=0
    g25: GeomPoint X=4e-15 Y=32.0588 Z=0
    g26: GeomPoint X=-1e-16 Y=-40.7255 Z=0
  constraints (50):
    c: Horizontal(g0)
    c: Symmetric(g0,g0,g-1)
    c: Coincident(g1,g0)
    c: Vertical(g1)
    c: Coincident(g2,g0)
    c: Vertical(g2)
    c: Coincident(g3,g1)
    c: Coincident(g3,g2)
    c: Horizontal(g3)
    c: Coincident(g4,g2)
    c: Coincident(g5,g1)
    c: InternalAlignment(g7-g10 -> g6) x4
    c: PointOnObject(g6,g-2)
    c: Coincident(g11,g5)
    c: Coincident(g11,g4)
    c: Horizontal(g11)
    c: Coincident(g12,g1)
    c: PointOnObject(g12,g11)
    c: Vertical(g12)
    c: Coincident(g13,g2)
    c: PointOnObject(g13,g11)
    c: Vertical(g13)
    c: PointOnObject(g7,g-2)
    c: Coincident(g14,g6)
    c: Coincident(g14,g6)
    c: Coincident(g6,g5)
    c: Coincident(g6,g4)
    c: DistanceY(g0,g2) = 3.6
    c: DistanceY(g-1,g4) = 11
    c: DistanceX(g5,g4) = 30.6667
    c: DistanceX(g0,g0) = 25.5833
    c: DistanceY(g-1,g7) = 35.6667
    c: DistanceY(g8,g7) = 40
    c: InternalAlignment(g16-g19 -> g15) x4
    c: DistanceY(g17,g16) = 40
    c: Vertical(g16)
    c: PointOnObject(g16,g-2)
    c: PointOnObject(g15,g11)
    c: PointOnObject(g15,g11)
    c: DistanceX(g15,g4) = 1.2
    c: DistanceY(g16,g7) = 1.2
    c: Coincident(g20,g15)
    c: Coincident(g20,g5)
    c: Coincident(g21,g15)
    c: Coincident(g21,g4)
    c: InternalAlignment(g23-g26 -> g22) x4
    c: DistanceY(g22,g23) = 40
    c: Coincident(g22,g20)
    c: Coincident(g22,g21)
    c: Coincident(g23,g7)
FEATURE [PartDesign::Plane] DatumPlane004  label="Datum_EarTrim"
  AttachmentOffset = pos=(0,0,-4) rot=(0,0,1;0rad)
  Length = 61.2949
  MapMode = 5
  Placement = pos=(0,4,9e-16) rot=(1,0,0;1.5708rad)
  ResizeMode = 0
  Support = -> [XZ_Plane001]
  Width = 75.0828
  expr: .AttachmentOffset.Base.z = -1 * <<params>>.ear_trim_leng
FEATURE [Sketcher::SketchObject] Sketch022  label="Sketch_EarTrimF"
  FullyConstrained = true
  MapMode = 5
  Placement = pos=(0,0,0) rot=(1,0,0;1.5708rad)
  Support = -> [XZ_Plane001]
  expr: Constraints[64] = <<params>>.ear_trim_thick
  expr: Constraints[47] = <<params>>.ear_trim_thick
  expr: Constraints[46] = <<params>>.ear_trim_thick
  expr: Constraints[30] = <<params>>.ear_base_thick + <<params>>.ear_vert_height
  expr: Constraints[31] = <<params>>.ear_front_mid_height
  expr: Constraints[32] = <<params>>.ear_front_mid_width
  expr: Constraints[48] = <<params>>.ear_ellipse_majax
  expr: Constraints[33] = <<params>>.ear_front_base_width
  expr: Constraints[34] = <<params>>.ear_front_tot_height
  expr: Constraints[35] = <<params>>.ear_ellipse_majax
  sketch-geometry (27):
    g0: LineSegment StartX=-13 StartY=0 StartZ=0 EndX=13 EndY=0 EndZ=0
    g1: LineSegment StartX=-13 StartY=0 StartZ=0 EndX=-13 EndY=3.6 EndZ=0
    g2: LineSegment StartX=13 StartY=0 StartZ=0 EndX=13 EndY=3.6 EndZ=0
    g3: LineSegment StartX=-13 StartY=3.6 StartZ=0 EndX=13 EndY=3.6 EndZ=0
    g4: LineSegment StartX=13 StartY=3.6 StartZ=0 EndX=16 EndY=12 EndZ=0
    g5: LineSegment StartX=-13 StartY=3.6 StartZ=0 EndX=-16 EndY=12 EndZ=0
    g6: ArcOfEllipse CenterX=0 CenterY=-3.2e-15 CenterZ=0 NormalX=0 NormalY=0 NormalZ=1 MajorRadius=40 MinorRadius=16.7726 AngleXU=1.5708 StartAngle=5.01708 EndAngle=7.54929
    g7: LineSegment StartX=0 StartY=40 StartZ=0 EndX=0 EndY=-40 EndZ=0
    g8: LineSegment StartX=-16.7726 StartY=-3.2e-15 StartZ=0 EndX=16.7726 EndY=-3.2e-15 EndZ=0
    g9: GeomPoint X=4e-15 Y=36.3137 Z=0
    g10: GeomPoint X=0 Y=-36.3137 Z=0
    g11: LineSegment StartX=-16 StartY=12 StartZ=0 EndX=16 EndY=12 EndZ=0
    g12: LineSegment StartX=-13 StartY=3.6 StartZ=0 EndX=-13 EndY=12 EndZ=0
    g13: LineSegment StartX=13 StartY=3.6 StartZ=0 EndX=13 EndY=12 EndZ=0
    g14: LineSegment StartX=-16 StartY=12 StartZ=0 EndX=16 EndY=12 EndZ=0
    g15: ArcOfEllipse CenterX=-1.8e-15 CenterY=-1.2 CenterZ=0 NormalX=0 NormalY=0 NormalZ=1 MajorRadius=40 MinorRadius=15.6783 AngleXU=1.5708 StartAngle=5.04869 EndAngle=7.51768
    g16: LineSegment StartX=-1.7e-15 StartY=38.8 StartZ=0 EndX=-1.7e-15 EndY=-41.2 EndZ=0
    g17: LineSegment StartX=-15.6783 StartY=-1.2 StartZ=0 EndX=15.6783 EndY=-1.2 EndZ=0
    g18: GeomPoint X=2.3e-15 Y=35.5993 Z=0
    g19: GeomPoint X=-1.7e-15 Y=-37.9993 Z=0
    g20: LineSegment StartX=-16 StartY=12 StartZ=0 EndX=-14.8 EndY=12 EndZ=0
    g21: LineSegment StartX=16 StartY=12 StartZ=0 EndX=14.8 EndY=12 EndZ=0
    g22: LineSegment StartX=-16 StartY=12 StartZ=0 EndX=-17.2 EndY=12 EndZ=0
    g23: LineSegment StartX=16 StartY=12 StartZ=0 EndX=17.2 EndY=12 EndZ=0
    g24: LineSegment StartX=17.2 StartY=12 StartZ=0 EndX=17.2 EndY=41.2 EndZ=0
    g25: LineSegment StartX=17.2 StartY=41.2 StartZ=0 EndX=-17.2 EndY=41.2 EndZ=0
    g26: LineSegment StartX=-17.2 StartY=41.2 StartZ=0 EndX=-17.2 EndY=12 EndZ=0
  constraints (59):
    c: Horizontal(g0)
    c: Symmetric(g0,g0,g-1)
    c: Coincident(g1,g0)
    c: Vertical(g1)
    c: Coincident(g2,g0)
    c: Vertical(g2)
    c: Coincident(g3,g1)
    c: Coincident(g3,g2)
    c: Horizontal(g3)
    c: Coincident(g4,g2)
    c: Coincident(g5,g1)
    c: InternalAlignment(g7-g10 -> g6) x4
    c: PointOnObject(g6,g-2)
    c: Coincident(g11,g5)
    c: Coincident(g11,g4)
    c: Horizontal(g11)
    c: Coincident(g12,g1)
    c: PointOnObject(g12,g11)
    c: Vertical(g12)
    c: Coincident(g13,g2)
    c: PointOnObject(g13,g11)
    c: Vertical(g13)
    c: PointOnObject(g7,g-2)
    c: Coincident(g14,g6)
    c: Coincident(g14,g6)
    c: Coincident(g6,g5)
    c: Coincident(g6,g4)
    c: DistanceY(g0,g2) = 3.6
    c: DistanceY(g-1,g4) = 12
    c: DistanceX(g5,g4) = 32
    c: DistanceX(g0,g0) = 26
    c: DistanceY(g-1,g7) = 40
    c: DistanceY(g8,g7) = 40
    c: InternalAlignment(g16-g19 -> g15) x4
    c: Vertical(g16)
    c: PointOnObject(g20,g11)
    c: PointOnObject(g21,g11)
    c: Coincident(g15,g20)
    c: Coincident(g15,g21)
    c: Equal(g21,g20)
    c: DistanceX(g15,g4) = 1.2
    c: DistanceY(g16,g7) = 1.2
    c: DistanceY(g17,g16) = 40
    c: Coincident(g22,g20)
    c: Horizontal(g22)
    c: Coincident(g23,g21)
    c: Horizontal(g23)
    c: Coincident(g24,g23)
    c: Vertical(g24)
    c: Coincident(g25,g24)
    c: Horizontal(g25)
    c: Coincident(g26,g25)
    c: Coincident(g26,g22)
    c: Vertical(g26)
    c: Equal(g21,g23)
    c: Equal(g20,g22)
    c: Coincident(g20,g5)
    c: Coincident(g21,g4)
    c: DistanceY(g7,g24) = 1.2
FEATURE [Sketcher::SketchObject] Sketch023  label="Sketch_EarTrimB"
  FullyConstrained = true
  MapMode = 5
  Placement = pos=(0,4,9e-16) rot=(1,0,0;1.5708rad)
  Support = -> [DatumPlane004]
  expr: Constraints[32] = <<params>>.ear_trim_mid_width
  expr: Constraints[64] = <<params>>.ear_trim_thick
  expr: Constraints[35] = <<params>>.ear_ellipse_majax
  expr: Constraints[34] = <<params>>.ear_trim_tot_height
  expr: Constraints[33] = <<params>>.ear_front_base_width
  expr: Constraints[48] = <<params>>.ear_ellipse_majax
  expr: Constraints[31] = <<params>>.ear_trim_mid_height
  expr: Constraints[30] = <<params>>.ear_base_thick + <<params>>.ear_vert_height
  expr: Constraints[46] = <<params>>.ear_trim_thick
  expr: Constraints[47] = <<params>>.ear_trim_thick
  sketch-geometry (27):
    g0: LineSegment StartX=-13 StartY=0 StartZ=0 EndX=13 EndY=0 EndZ=0
    g1: LineSegment StartX=-13 StartY=0 StartZ=0 EndX=-13 EndY=3.6 EndZ=0
    g2: LineSegment StartX=13 StartY=0 StartZ=0 EndX=13 EndY=3.6 EndZ=0
    g3: LineSegment StartX=-13 StartY=3.6 StartZ=0 EndX=13 EndY=3.6 EndZ=0
    g4: LineSegment StartX=13 StartY=3.6 StartZ=0 EndX=15.3333 EndY=11 EndZ=0
    g5: LineSegment StartX=-13 StartY=3.6 StartZ=0 EndX=-15.3333 EndY=11 EndZ=0
    g6: ArcOfEllipse CenterX=0 CenterY=-4.33333 CenterZ=0 NormalX=0 NormalY=0 NormalZ=1 MajorRadius=40 MinorRadius=16.6015 AngleXU=1.5708 StartAngle=5.10579 EndAngle=7.46058
    g7: LineSegment StartX=0 StartY=35.6667 StartZ=0 EndX=0 EndY=-44.3333 EndZ=0
    g8: LineSegment StartX=-16.6015 StartY=-4.33333 StartZ=0 EndX=16.6015 EndY=-4.33333 EndZ=0
    g9: GeomPoint X=4e-15 Y=32.0588 Z=0
    g10: GeomPoint X=0 Y=-40.7255 Z=0
    g11: LineSegment StartX=-15.3333 StartY=11 StartZ=0 EndX=15.3333 EndY=11 EndZ=0
    g12: LineSegment StartX=-13 StartY=3.6 StartZ=0 EndX=-13 EndY=11 EndZ=0
    g13: LineSegment StartX=13 StartY=3.6 StartZ=0 EndX=13 EndY=11 EndZ=0
    g14: LineSegment StartX=-15.3333 StartY=11 StartZ=0 EndX=15.3333 EndY=11 EndZ=0
    g15: ArcOfEllipse CenterX=-2.7e-15 CenterY=-5.53333 CenterZ=0 NormalX=0 NormalY=0 NormalZ=1 MajorRadius=40 MinorRadius=15.5212 AngleXU=1.5708 StartAngle=5.1385 EndAngle=7.42787
    g16: LineSegment StartX=-2.9e-15 StartY=34.4667 StartZ=0 EndX=-2.9e-15 EndY=-45.5333 EndZ=0
    g17: LineSegment StartX=-15.5212 StartY=-5.53333 StartZ=0 EndX=15.5212 EndY=-5.53333 EndZ=0
    g18: GeomPoint X=1.4e-15 Y=31.3325 Z=0
    g19: GeomPoint X=-2.9e-15 Y=-42.3992 Z=0
    g20: LineSegment StartX=-15.3333 StartY=11 StartZ=0 EndX=-14.1333 EndY=11 EndZ=0
    g21: LineSegment StartX=15.3333 StartY=11 StartZ=0 EndX=14.1333 EndY=11 EndZ=0
    g22: LineSegment StartX=15.3333 StartY=11 StartZ=0 EndX=16.5333 EndY=11 EndZ=0
    g23: LineSegment StartX=16.5333 StartY=11 StartZ=0 EndX=16.5333 EndY=36.8667 EndZ=0
    g24: LineSegment StartX=16.5333 StartY=36.8667 StartZ=0 EndX=-16.5333 EndY=36.8667 EndZ=0
    g25: LineSegment StartX=-16.5333 StartY=36.8667 StartZ=0 EndX=-16.5333 EndY=11 EndZ=0
    g26: LineSegment StartX=-16.5333 StartY=11 StartZ=0 EndX=-15.3333 EndY=11 EndZ=0
  constraints (59):
    c: Horizontal(g0)
    c: Symmetric(g0,g0,g-1)
    c: Coincident(g1,g0)
    c: Vertical(g1)
    c: Coincident(g2,g0)
    c: Vertical(g2)
    c: Coincident(g3,g1)
    c: Coincident(g3,g2)
    c: Horizontal(g3)
    c: Coincident(g4,g2)
    c: Coincident(g5,g1)
    c: InternalAlignment(g7-g10 -> g6) x4
    c: PointOnObject(g6,g-2)
    c: Coincident(g11,g5)
    c: Coincident(g11,g4)
    c: Horizontal(g11)
    c: Coincident(g12,g1)
    c: PointOnObject(g12,g11)
    c: Vertical(g12)
    c: Coincident(g13,g2)
    c: PointOnObject(g13,g11)
    c: Vertical(g13)
    c: PointOnObject(g7,g-2)
    c: Coincident(g14,g6)
    c: Coincident(g14,g6)
    c: Coincident(g6,g5)
    c: Coincident(g6,g4)
    c: DistanceY(g0,g2) = 3.6
    c: DistanceY(g-1,g4) = 11
    c: DistanceX(g5,g4) = 30.6667
    c: DistanceX(g0,g0) = 26
    c: DistanceY(g-1,g7) = 35.6667
    c: DistanceY(g8,g7) = 40
    c: InternalAlignment(g16-g19 -> g15) x4
    c: Vertical(g16)
    c: PointOnObject(g20,g11)
    c: PointOnObject(g21,g11)
    c: Coincident(g15,g20)
    c: Coincident(g15,g21)
    c: Equal(g21,g20)
    c: DistanceX(g15,g4) = 1.2
    c: DistanceY(g16,g7) = 1.2
    c: DistanceY(g17,g16) = 40
    c: Coincident(g22,g21)
    c: Horizontal(g22)
    c: Coincident(g23,g22)
    c: Vertical(g23)
    c: Coincident(g24,g23)
    c: Horizontal(g24)
    c: Coincident(g25,g24)
    c: Vertical(g25)
    c: Coincident(g26,g25)
    c: Coincident(g26,g20)
    c: Horizontal(g26)
    c: Equal(g20,g26)
    c: Coincident(g20,g5)
    c: Equal(g22,g21)
    c: Coincident(g21,g4)
    c: DistanceY(g7,g23) = 1.2
FEATURE [PartDesign::SubtractiveLoft] SubtractiveLoft001  label="SubtractiveLoft_EarTrim"
  BaseFeature = -> Pocket009
  Closed = false
  Placement = pos=(0,0,0) rot=(1,0,0;1.5708rad)
  Profile = -> Sketch022
  Ruled = false
  Sections = -> [Sketch023]
FEATURE [Sketcher::SketchObject] Sketch024  label="Sketch_ClipHole"
  FullyConstrained = true
  MapMode = 5
  Placement = pos=(0,0,0) rot=(0.57735,0.57735,0.57735;2.0944rad)
  Support = -> [YZ_Plane001]
  expr: Constraints[9] = <<params>>.ear_trim_clip_height + <<params>>.ear_trim_clip_tol
  expr: Constraints[10] = Spreadsheet.ear_trim_clip_width + <<params>>.ear_trim_clip_tol
  expr: Constraints[11] = <<params>>.ear_trim_leng
  expr: Constraints[12] = <<params>>.ear_front_mid_height + <<params>>.ear_trim_clip_height + <<params>>.ear_trim_clip_tol / 2
  sketch-geometry (5):
    g0: LineSegment StartX=2.2 StartY=16.7 StartZ=0 EndX=4 EndY=16.7 EndZ=0
    g1: LineSegment StartX=4 StartY=16.7 StartZ=0 EndX=4 EndY=13.5 EndZ=0
    g2: LineSegment StartX=4 StartY=13.5 StartZ=0 EndX=2.2 EndY=13.5 EndZ=0
    g3: LineSegment StartX=2.2 StartY=13.5 StartZ=0 EndX=2.2 EndY=16.7 EndZ=0
    g4: GeomPoint X=3.1 Y=15.1 Z=0
  constraints (13):
    c: Coincident(g0,g1)
    c: Coincident(g1,g2)
    c: Coincident(g2,g3)
    c: Coincident(g3,g0)
    c: Horizontal(g0)
    c: Horizontal(g2)
    c: Vertical(g1)
    c: Vertical(g3)
    c: Symmetric(g2,g0,g4)
    c: DistanceY(g2,g0) = 3.2
    c: DistanceX(g2,g1) = 1.8
    c: DistanceX(g-1,g0) = 4
    c: DistanceY(g-1,g4) = 15.1
FEATURE [PartDesign::Pocket] Pocket010  label="Pocket_EarTrimMtSlot"
  BaseFeature = -> SubtractiveLoft001
  Length = 5
  Length2 = 100
  Midplane = true
  Placement = pos=(0,0,0) rot=(1,0,0;1.5708rad)
  Profile = -> Sketch024
  Type = 1
FEATURE [PartDesign::AdditiveLoft] AdditiveLoft001  label="AdditiveLoft_EarTrimMain"
  Closed = false
  Placement = pos=(0,0,0) rot=(1,0,0;1.5708rad)
  Profile = -> Sketch020
  Ruled = false
  Sections = -> [Sketch021]
FEATURE [Sketcher::SketchObject] Sketch025  label="Sketch_ClipSplit_Top"
  FullyConstrained = true
  MapMode = 5
  Placement = pos=(0,0,0) rot=(0.57735,0.57735,0.57735;2.0944rad)
  Support = -> [YZ_Plane009]
  expr: Constraints[8] = <<params>>.ear_trim_leng
  expr: Constraints[25] = <<params>>.ear_front_mid_height + <<params>>.ear_trim_clip_height + <<params>>.ear_trim_clip_tol / 2
  expr: Constraints[28] = <<params>>.ear_trim_clip_thick + <<params>>.ear_trim_clip_wedge_size
  expr: Constraints[26] = <<params>>.ear_trim_clip_width
  expr: Constraints[27] = <<params>>.ear_trim_clip_height - 2 * <<params>>.ear_trim_clip_thick
  sketch-geometry (11):
    g0: LineSegment StartX=2.4 StartY=17 StartZ=0 EndX=4 EndY=17 EndZ=0
    g1: LineSegment StartX=4 StartY=17 StartZ=0 EndX=4 EndY=15.8 EndZ=0
    g2: LineSegment StartX=4 StartY=15.8 StartZ=0 EndX=2.4 EndY=15.8 EndZ=0
    g3: LineSegment StartX=2.4 StartY=15.8 StartZ=0 EndX=2.4 EndY=17 EndZ=0
    g4: GeomPoint X=3.2 Y=15.1 Z=0
    g5: LineSegment StartX=2.4 StartY=14.4 StartZ=0 EndX=4 EndY=14.4 EndZ=0
    g6: LineSegment StartX=4 StartY=14.4 StartZ=0 EndX=4 EndY=13.2 EndZ=0
    g7: LineSegment StartX=4 StartY=13.2 StartZ=0 EndX=2.4 EndY=13.2 EndZ=0
    g8: LineSegment StartX=2.4 StartY=13.2 StartZ=0 EndX=2.4 EndY=14.4 EndZ=0
    g9: LineSegment StartX=2.4 StartY=15.8 StartZ=0 EndX=2.4 EndY=14.4 EndZ=0
    g10: LineSegment StartX=4 StartY=15.8 StartZ=0 EndX=4 EndY=14.4 EndZ=0
  constraints (29):
    c: Coincident(g0,g1)
    c: Coincident(g1,g2)
    c: Coincident(g2,g3)
    c: Coincident(g3,g0)
    c: Horizontal(g0)
    c: Horizontal(g2)
    c: Vertical(g1)
    c: Vertical(g3)
    c: DistanceX(g-1,g1) = 4
    c: Coincident(g5,g6)
    c: Coincident(g6,g7)
    c: Coincident(g7,g8)
    c: Coincident(g8,g5)
    c: Horizontal(g5)
    c: Horizontal(g7)
    c: Vertical(g6)
    c: Vertical(g8)
    c: Coincident(g9,g2)
    c: Coincident(g9,g5)
    c: Coincident(g10,g1)
    c: Coincident(g10,g5)
    c: Vertical(g10)
    c: Vertical(g9)
    c: Symmetric(g1,g5,g4)
    c: Equal(g3,g8)
    c: DistanceY(g-1,g4) = 15.1
    c: DistanceX(g7,g6) = 1.6
    c: DistanceY(g5,g1) = 1.4
    c: DistanceY(g1,g0) = 1.2
FEATURE [PartDesign::Pad] Pad009  label="Pad_ClipTop"
  BaseFeature = -> AdditiveLoft001
  Direction = (1,1,1)
  Length = 40
  Length2 = 100
  Midplane = true
  Placement = pos=(0,0,0) rot=(1,0,0;1.5708rad)
  Profile = -> Sketch025
  Type = 0
  expr: Length = <<params>>.ear_front_mid_width * 1.25
FEATURE [Sketcher::SketchObject] Sketch026  label="Sketch_ClipSplit_Bot"
  FullyConstrained = true
  MapMode = 5
  Placement = pos=(0,0,0) rot=(0.57735,0.57735,0.57735;2.0944rad)
  Support = -> [YZ_Plane009]
  expr: Constraints[27] = <<params>>.ear_trim_clip_height - 2 * <<params>>.ear_trim_clip_thick
  expr: Constraints[26] = <<params>>.ear_trim_clip_width
  expr: Constraints[28] = <<params>>.ear_trim_clip_thick + <<params>>.ear_trim_clip_wedge_size
  expr: Constraints[25] = <<params>>.ear_front_mid_height + <<params>>.ear_trim_clip_height + <<params>>.ear_trim_clip_tol / 2
  expr: Constraints[8] = <<params>>.ear_trim_leng
  sketch-geometry (11):
    g0: LineSegment StartX=2.4 StartY=17 StartZ=0 EndX=4 EndY=17 EndZ=0
    g1: LineSegment StartX=4 StartY=17 StartZ=0 EndX=4 EndY=15.8 EndZ=0
    g2: LineSegment StartX=4 StartY=15.8 StartZ=0 EndX=2.4 EndY=15.8 EndZ=0
    g3: LineSegment StartX=2.4 StartY=15.8 StartZ=0 EndX=2.4 EndY=17 EndZ=0
    g4: GeomPoint X=3.2 Y=15.1 Z=0
    g5: LineSegment StartX=2.4 StartY=14.4 StartZ=0 EndX=4 EndY=14.4 EndZ=0
    g6: LineSegment StartX=4 StartY=14.4 StartZ=0 EndX=4 EndY=13.2 EndZ=0
    g7: LineSegment StartX=4 StartY=13.2 StartZ=0 EndX=2.4 EndY=13.2 EndZ=0
    g8: LineSegment StartX=2.4 StartY=13.2 StartZ=0 EndX=2.4 EndY=14.4 EndZ=0
    g9: LineSegment StartX=2.4 StartY=15.8 StartZ=0 EndX=2.4 EndY=14.4 EndZ=0
    g10: LineSegment StartX=4 StartY=15.8 StartZ=0 EndX=4 EndY=14.4 EndZ=0
  constraints (29):
    c: Coincident(g0,g1)
    c: Coincident(g1,g2)
    c: Coincident(g2,g3)
    c: Coincident(g3,g0)
    c: Horizontal(g0)
    c: Horizontal(g2)
    c: Vertical(g1)
    c: Vertical(g3)
    c: DistanceX(g-1,g1) = 4
    c: Coincident(g5,g6)
    c: Coincident(g6,g7)
    c: Coincident(g7,g8)
    c: Coincident(g8,g5)
    c: Horizontal(g5)
    c: Horizontal(g7)
    c: Vertical(g6)
    c: Vertical(g8)
    c: Coincident(g9,g2)
    c: Coincident(g9,g5)
    c: Coincident(g10,g1)
    c: Coincident(g10,g5)
    c: Vertical(g10)
    c: Vertical(g9)
    c: Symmetric(g1,g5,g4)
    c: Equal(g3,g8)
    c: DistanceY(g-1,g4) = 15.1
    c: DistanceX(g7,g6) = 1.6
    c: DistanceY(g5,g1) = 1.4
    c: DistanceY(g1,g0) = 1.2
FEATURE [PartDesign::Pad] Pad010  label="Pad_ClipBot"
  BaseFeature = -> Pad009
  Direction = (1,1,1)
  Length = 40
  Length2 = 100
  Midplane = true
  Placement = pos=(0,0,0) rot=(1,0,0;1.5708rad)
  Profile = -> Sketch026
  Type = 0
  expr: Length = <<params>>.ear_front_mid_width * 1.25
FEATURE [Sketcher::SketchObject] Sketch027  label="Sketch_EarClipFront"
  FullyConstrained = true
  MapMode = 5
  Placement = pos=(0,0,0) rot=(1,0,0;1.5708rad)
  Support = -> [XZ_Plane009]
  expr: Constraints[35] = <<params>>.ear_ellipse_majax
  expr: Constraints[60] = <<params>>.ear_trim_clip_thick
  expr: Constraints[40] = <<params>>.ear_ellipse_majax
  expr: Constraints[32] = <<params>>.ear_front_mid_width
  expr: Constraints[34] = <<params>>.ear_front_tot_height
  expr: Constraints[46] = <<params>>.ear_trim_thick
  expr: Constraints[93] = <<params>>.ear_trim_clip_leng
  expr: Constraints[141] = <<params>>.ear_ellipse_majax
  expr: Constraints[94] = <<params>>.ear_trim_clip_leng
  expr: Constraints[113] = <<params>>.ear_trim_clip_thick + <<params>>.ear_trim_clip_wedge_size
  expr: Constraints[45] = <<params>>.ear_trim_thick
  expr: Constraints[33] = <<params>>.ear_front_base_width
  expr: Constraints[138] = <<params>>.ear_front_mid_height + <<params>>.ear_trim_clip_height + <<params>>.ear_trim_clip_tol / 2
  expr: Constraints[31] = <<params>>.ear_front_mid_height
  expr: Constraints[30] = <<params>>.ear_base_thick + <<params>>.ear_vert_height
  expr: Constraints[140] = <<params>>.ear_trim_clip_height
  sketch-geometry (69):
    g0: LineSegment StartX=-13 StartY=0 StartZ=0 EndX=13 EndY=0 EndZ=0
    g1: LineSegment StartX=-13 StartY=0 StartZ=0 EndX=-13 EndY=3.6 EndZ=0
    g2: LineSegment StartX=13 StartY=0 StartZ=0 EndX=13 EndY=3.6 EndZ=0
    g3: LineSegment StartX=-13 StartY=3.6 StartZ=0 EndX=13 EndY=3.6 EndZ=0
    g4: LineSegment StartX=13 StartY=3.6 StartZ=0 EndX=16 EndY=12 EndZ=0
    g5: LineSegment StartX=-13 StartY=3.6 StartZ=0 EndX=-16 EndY=12 EndZ=0
    g6: ArcOfEllipse CenterX=0 CenterY=4e-16 CenterZ=0 NormalX=0 NormalY=0 NormalZ=1 MajorRadius=40 MinorRadius=16.7726 AngleXU=1.5708 StartAngle=5.01708 EndAngle=7.54929
    g7: LineSegment StartX=0 StartY=40 StartZ=0 EndX=0 EndY=-40 EndZ=0
    g8: LineSegment StartX=-16.7726 StartY=4e-16 StartZ=0 EndX=16.7726 EndY=4e-16 EndZ=0
    g9: GeomPoint X=4e-15 Y=36.3137 Z=0
    g10: GeomPoint X=0 Y=-36.3137 Z=0
    g11: LineSegment StartX=-16 StartY=12 StartZ=0 EndX=16 EndY=12 EndZ=0
    g12: LineSegment StartX=-13 StartY=3.6 StartZ=0 EndX=-13 EndY=12 EndZ=0
    g13: LineSegment StartX=13 StartY=3.6 StartZ=0 EndX=13 EndY=12 EndZ=0
    g14: LineSegment StartX=-16 StartY=12 StartZ=0 EndX=16 EndY=12 EndZ=0
    g15: ArcOfEllipse CenterX=0 CenterY=-1.2 CenterZ=0 NormalX=0 NormalY=0 NormalZ=1 MajorRadius=40 MinorRadius=15.6783 AngleXU=1.5708 StartAngle=5.04869 EndAngle=7.51768
    g16: LineSegment StartX=0 StartY=38.8 StartZ=0 EndX=0 EndY=-41.2 EndZ=0
    g17: LineSegment StartX=-15.6783 StartY=-1.2 StartZ=0 EndX=15.6783 EndY=-1.2 EndZ=0
    g18: GeomPoint X=4.1e-15 Y=35.5993 Z=0
    g19: GeomPoint X=0 Y=-37.9993 Z=0
    g20: LineSegment StartX=-14.0404 StartY=16.6 StartZ=0 EndX=-12.6404 EndY=16.6 EndZ=0
    g21: LineSegment StartX=-14.1919 StartY=15.8 StartZ=0 EndX=-11.8404 EndY=15.8 EndZ=0
    g22: LineSegment StartX=-12.6404 StartY=16.6 StartZ=0 EndX=-12.6404 EndY=15.8 EndZ=0
    g23: LineSegment StartX=-11.8404 StartY=15.8 StartZ=0 EndX=-11.8404 EndY=16.6 EndZ=0
    g24: LineSegment StartX=-11.8404 StartY=16.6 StartZ=0 EndX=-12.2404 EndY=17 EndZ=0
    g25: LineSegment StartX=-12.6404 StartY=16.6 StartZ=0 EndX=-11.8404 EndY=16.6 EndZ=0
    g26: LineSegment StartX=-12.6404 StartY=16.6 StartZ=0 EndX=-12.2404 EndY=17 EndZ=0
    g27: LineSegment StartX=14.0404 StartY=16.6 StartZ=0 EndX=12.6404 EndY=16.6 EndZ=0
    g28: LineSegment StartX=14.1919 StartY=15.8 StartZ=0 EndX=12.6404 EndY=15.8 EndZ=0
    g29: LineSegment StartX=12.6404 StartY=16.6 StartZ=0 EndX=12.2404 EndY=17 EndZ=0
    g30: LineSegment StartX=12.2404 StartY=17 StartZ=0 EndX=11.8404 EndY=16.6 EndZ=0
    g31: LineSegment StartX=11.8404 StartY=16.6 StartZ=0 EndX=11.8404 EndY=15.8 EndZ=0
    g32: LineSegment StartX=11.8404 StartY=15.8 StartZ=0 EndX=12.6404 EndY=15.8 EndZ=0
    g33: LineSegment StartX=12.6404 StartY=16.6 StartZ=0 EndX=12.6404 EndY=15.8 EndZ=0
    g34: LineSegment StartX=11.8404 StartY=16.6 StartZ=0 EndX=12.6404 EndY=16.6 EndZ=0
    g35: LineSegment StartX=-11.8404 StartY=16.6 StartZ=0 EndX=11.8404 EndY=16.6 EndZ=0
    g36: LineSegment StartX=-11.8404 StartY=15.8 StartZ=0 EndX=11.8404 EndY=15.8 EndZ=0
    g37: LineSegment StartX=-12.2404 StartY=17 StartZ=0 EndX=12.2404 EndY=17 EndZ=0
    g38: LineSegment StartX=-14.8 StartY=12 StartZ=0 EndX=14.8 EndY=12 EndZ=0
    g39: LineSegment StartX=-14.4368 StartY=14.4 StartZ=0 EndX=-14.1919 EndY=15.8 EndZ=0
    g40: LineSegment StartX=-14.0404 StartY=16.6 StartZ=0 EndX=-14.0404 EndY=13.6 EndZ=0
    g41: ArcOfEllipse CenterX=4e-15 CenterY=-1.2 CenterZ=0 NormalX=0 NormalY=0 NormalZ=1 MajorRadius=40 MinorRadius=15.6783 AngleXU=1.5708 StartAngle=5.17356 EndAngle=7.39281
    g42: LineSegment StartX=0 StartY=38.8 StartZ=0 EndX=7.9e-15 EndY=-41.2 EndZ=0
    g43: LineSegment StartX=-15.6783 StartY=-1.2 StartZ=0 EndX=15.6783 EndY=-1.2 EndZ=0
    g44: GeomPoint X=-4.2e-15 Y=35.5993 Z=0
    g45: GeomPoint X=7.5e-15 Y=-37.9993 Z=0
    g46: GeomPoint X=-14.0404 Y=15.1 Z=0
    g47: LineSegment StartX=-12.2404 StartY=17 StartZ=0 EndX=-12.2404 EndY=15.8 EndZ=0
    g48: LineSegment StartX=-14.4368 StartY=14.4 StartZ=0 EndX=-13.0368 EndY=14.4 EndZ=0
    g49: LineSegment StartX=-14.5656 StartY=13.6 StartZ=0 EndX=-13.0368 EndY=13.6 EndZ=0
    g50: LineSegment StartX=-13.0368 StartY=14.4 StartZ=0 EndX=-12.2368 EndY=14.4 EndZ=0
    g51: LineSegment StartX=-13.0368 StartY=13.6 StartZ=0 EndX=-12.6368 EndY=13.2 EndZ=0
    g52: LineSegment StartX=-12.6368 StartY=13.2 StartZ=0 EndX=-12.2368 EndY=13.6 EndZ=0
    g53: LineSegment StartX=-12.2368 StartY=13.6 StartZ=0 EndX=-12.2368 EndY=14.4 EndZ=0
    g54: LineSegment StartX=-13.0368 StartY=14.4 StartZ=0 EndX=-13.0368 EndY=13.6 EndZ=0
    g55: LineSegment StartX=-13.0368 StartY=13.6 StartZ=0 EndX=-12.2368 EndY=13.6 EndZ=0
    g56: LineSegment StartX=-12.6368 StartY=13.2 StartZ=0 EndX=-12.6368 EndY=14.4 EndZ=0
    g57: LineSegment StartX=-14.5656 StartY=13.6 StartZ=0 EndX=-14.8 EndY=12 EndZ=0
    g58: LineSegment StartX=14.4368 StartY=14.4 StartZ=0 EndX=13.0368 EndY=14.4 EndZ=0
    g59: LineSegment StartX=13.0368 StartY=14.4 StartZ=0 EndX=12.2368 EndY=14.4 EndZ=0
    g60: LineSegment StartX=12.2368 StartY=14.4 StartZ=0 EndX=12.2368 EndY=13.6 EndZ=0
    g61: LineSegment StartX=12.2368 StartY=13.6 StartZ=0 EndX=12.6368 EndY=13.2 EndZ=0
    g62: LineSegment StartX=12.6368 StartY=13.2 StartZ=0 EndX=13.0368 EndY=13.6 EndZ=0
    g63: LineSegment StartX=13.0368 StartY=13.6 StartZ=0 EndX=14.5656 EndY=13.6 EndZ=0
    g64: LineSegment StartX=13.0368 StartY=13.6 StartZ=0 EndX=13.0368 EndY=14.4 EndZ=0
    g65: LineSegment StartX=12.2368 StartY=13.6 StartZ=0 EndX=13.0368 EndY=13.6 EndZ=0
    g66: LineSegment StartX=-12.2368 StartY=14.4 StartZ=0 EndX=12.2368 EndY=14.4 EndZ=0
    g67: LineSegment StartX=14.1919 StartY=15.8 StartZ=0 EndX=14.4368 EndY=14.4 EndZ=0
    g68: LineSegment StartX=14.5656 StartY=13.6 StartZ=0 EndX=14.8 EndY=12 EndZ=0
  constraints (164):
    c: Horizontal(g0)
    c: Symmetric(g0,g0,g-1)
    c: Coincident(g1,g0)
    c: Vertical(g1)
    c: Coincident(g2,g0)
    c: Vertical(g2)
    c: Coincident(g3,g1)
    c: Coincident(g3,g2)
    c: Horizontal(g3)
    c: Coincident(g4,g2)
    c: Coincident(g5,g1)
    c: InternalAlignment(g7-g10 -> g6) x4
    c: PointOnObject(g6,g-2)
    c: Coincident(g11,g5)
    c: Coincident(g11,g4)
    c: Horizontal(g11)
    c: Coincident(g12,g1)
    c: PointOnObject(g12,g11)
    c: Vertical(g12)
    c: Coincident(g13,g2)
    c: PointOnObject(g13,g11)
    c: Vertical(g13)
    c: PointOnObject(g7,g-2)
    c: Coincident(g14,g6)
    c: Coincident(g14,g6)
    c: Coincident(g6,g5)
    c: Coincident(g6,g4)
    c: DistanceY(g0,g2) = 3.6
    c: DistanceY(g-1,g4) = 12
    c: DistanceX(g5,g4) = 32
    c: DistanceX(g0,g0) = 26
    c: DistanceY(g-1,g7) = 40
    c: DistanceY(g8,g7) = 40
    c: InternalAlignment(g16-g19 -> g15) x4
    c: DistanceY(g17,g16) = 40
    c: Vertical(g16)
    c: PointOnObject(g16,g-2)
    c: PointOnObject(g15,g11)
    c: PointOnObject(g15,g11)
    c: DistanceX(g15,g4) = 1.2
    c: DistanceY(g16,g7) = 1.2
    c: PointOnObject(g20,g15)
    c: Horizontal(g20)
    c: PointOnObject(g21,g15)
    c: Horizontal(g21)
    c: Coincident(g22,g20)
    c: PointOnObject(g22,g21)
    c: Vertical(g22)
    c: Coincident(g23,g21)
    c: Vertical(g23)
    c: Coincident(g24,g23)
    c: Coincident(g25,g20)
    c: Coincident(g25,g23)
    c: Horizontal(g25)
    c: DistanceY(g21,g23) = 0.8
    c: Coincident(g26,g20)
    c: Coincident(g26,g24)
    c: Equal(g24,g26)
    c: Angle(g26,g24) = 1.5708
    c: PointOnObject(g27,g15)
    c: Horizontal(g27)
    c: PointOnObject(g28,g15)
    c: Horizontal(g28)
    c: Coincident(g29,g27)
    c: Coincident(g30,g29)
    c: Coincident(g31,g30)
    c: Vertical(g31)
    c: Coincident(g32,g31)
    c: Coincident(g32,g28)
    c: Coincident(g33,g27)
    c: Coincident(g33,g28)
    c: Coincident(g34,g30)
    c: Coincident(g34,g27)
    c: Horizontal(g34)
    c: Vertical(g33)
    c: Horizontal(g32)
    c: Coincident(g35,g23)
    c: Coincident(g35,g30)
    c: Horizontal(g35)
    c: Coincident(g36,g21)
    c: Coincident(g36,g31)
    c: Horizontal(g36)
    c: Angle(g30,g29) = 1.5708
    c: Coincident(g37,g24)
    c: Coincident(g37,g29)
    c: Horizontal(g37)
    c: Equal(g24,g30)
    c: DistanceX(g20,g20) = 1.4
    c: DistanceX(g27,g27) = 1.4
    c: Coincident(g38,g15)
    c: Coincident(g38,g15)
    c: PointOnObject(g39,g15)
    c: PointOnObject(g49,g15)
    c: Coincident(g39,g21)
    c: Coincident(g40,g20)
    c: Vertical(g40)
    c: InternalAlignment(g42-g45 -> g41) x4
    c: Coincident(g42,g16)
    c: Coincident(g41,g20)
    c: Coincident(g41,g27)
    c: Symmetric(g20,g40,g46)
    c: Coincident(g47,g24)
    c: PointOnObject(g47,g21)
    c: Vertical(g47)
    c: DistanceY(g21,g24) = 1.2
    c: Coincident(g48,g39)
    c: Horizontal(g48)
    c: Horizontal(g49)
    c: PointOnObject(g40,g49)
    c: Coincident(g50,g48)
    c: Horizontal(g50)
    c: Coincident(g51,g49)
    c: Coincident(g52,g51)
    c: Coincident(g53,g52)
    c: Coincident(g53,g50)
    c: Vertical(g53)
    c: Coincident(g54,g48)
    c: Coincident(g54,g49)
    c: Coincident(g55,g49)
    c: Coincident(g55,g52)
    c: Horizontal(g55)
    c: Vertical(g54)
    c: Angle(g52,g51) = 1.5708
    c: Coincident(g56,g51)
    c: PointOnObject(g56,g50)
    c: Vertical(g56)
    c: Equal(g52,g51)
    c: Equal(g52,g24)
    c: Equal(g56,g47)
    c: DistanceY(g-1,g46) = 15.1
    c: Equal(g48,g20)
    c: DistanceY(g52,g23) = 3
    c: DistanceY(g43,g16) = 40
    c: Coincident(g57,g49)
    c: Coincident(g57,g38)
    c: PointOnObject(g58,g15)
    c: Horizontal(g58)
    c: Coincident(g59,g58)
    c: Horizontal(g59)
    c: Coincident(g60,g59)
    c: Vertical(g60)
    c: Coincident(g61,g60)
    c: Coincident(g62,g61)
    c: Coincident(g63,g62)
    c: PointOnObject(g63,g15)
    c: Horizontal(g63)
    c: Coincident(g64,g62)
    c: Coincident(g64,g58)
    c: Vertical(g64)
    c: Coincident(g65,g60)
    c: Coincident(g65,g62)
    c: Horizontal(g65)
    c: Angle(g62,g61) = 1.5708
    c: Equal(g29,g62)
    c: Equal(g61,g62)
    c: Equal(g60,g31)
    c: Equal(g58,g27)
    c: Coincident(g66,g50)
    c: Coincident(g66,g59)
    c: Horizontal(g66)
    c: Coincident(g67,g28)
    c: Coincident(g67,g58)
    c: Coincident(g68,g63)
    c: Coincident(g68,g38)
FEATURE [Sketcher::SketchObject] Sketch028  label="Sketch_EarClipBack"
  FullyConstrained = true
  MapMode = 5
  Placement = pos=(0,4,9e-16) rot=(1,0,0;1.5708rad)
  Support = -> [DatumPlane003]
  expr: Constraints[140] = <<params>>.ear_trim_clip_height
  expr: Constraints[30] = <<params>>.ear_base_thick + <<params>>.ear_vert_height
  expr: Constraints[31] = <<params>>.ear_trim_mid_height
  expr: Constraints[138] = <<params>>.ear_front_mid_height + <<params>>.ear_trim_clip_height + <<params>>.ear_trim_clip_tol / 2
  expr: Constraints[33] = <<params>>.ear_trim_base_width
  expr: Constraints[45] = <<params>>.ear_trim_thick
  expr: Constraints[113] = <<params>>.ear_trim_clip_thick + <<params>>.ear_trim_clip_wedge_size
  expr: Constraints[94] = <<params>>.ear_trim_clip_leng
  expr: Constraints[141] = <<params>>.ear_ellipse_majax
  expr: Constraints[93] = <<params>>.ear_trim_clip_leng
  expr: Constraints[46] = <<params>>.ear_trim_thick
  expr: Constraints[34] = <<params>>.ear_trim_tot_height
  expr: Constraints[32] = <<params>>.ear_trim_mid_width
  expr: Constraints[40] = <<params>>.ear_ellipse_majax
  expr: Constraints[60] = <<params>>.ear_trim_clip_thick
  expr: Constraints[35] = <<params>>.ear_ellipse_majax
  sketch-geometry (69):
    g0: LineSegment StartX=-12.7917 StartY=0 StartZ=0 EndX=12.7917 EndY=0 EndZ=0
    g1: LineSegment StartX=-12.7917 StartY=0 StartZ=0 EndX=-12.7917 EndY=3.6 EndZ=0
    g2: LineSegment StartX=12.7917 StartY=0 StartZ=0 EndX=12.7917 EndY=3.6 EndZ=0
    g3: LineSegment StartX=-12.7917 StartY=3.6 StartZ=0 EndX=12.7917 EndY=3.6 EndZ=0
    g4: LineSegment StartX=12.7917 StartY=3.6 StartZ=0 EndX=15.3333 EndY=11 EndZ=0
    g5: LineSegment StartX=-12.7917 StartY=3.6 StartZ=0 EndX=-15.3333 EndY=11 EndZ=0
    g6: ArcOfEllipse CenterX=0 CenterY=-4.33333 CenterZ=0 NormalX=0 NormalY=0 NormalZ=1 MajorRadius=40 MinorRadius=16.6015 AngleXU=1.5708 StartAngle=5.10579 EndAngle=7.46058
    g7: LineSegment StartX=0 StartY=35.6667 StartZ=0 EndX=0 EndY=-44.3333 EndZ=0
    g8: LineSegment StartX=-16.6015 StartY=-4.33333 StartZ=0 EndX=16.6015 EndY=-4.33333 EndZ=0
    g9: GeomPoint X=4e-15 Y=32.0588 Z=0
    g10: GeomPoint X=0 Y=-40.7255 Z=0
    g11: LineSegment StartX=-15.3333 StartY=11 StartZ=0 EndX=15.3333 EndY=11 EndZ=0
    g12: LineSegment StartX=-12.7917 StartY=3.6 StartZ=0 EndX=-12.7917 EndY=11 EndZ=0
    g13: LineSegment StartX=12.7917 StartY=3.6 StartZ=0 EndX=12.7917 EndY=11 EndZ=0
    g14: LineSegment StartX=-15.3333 StartY=11 StartZ=0 EndX=15.3333 EndY=11 EndZ=0
    g15: ArcOfEllipse CenterX=0 CenterY=-5.53333 CenterZ=0 NormalX=0 NormalY=0 NormalZ=1 MajorRadius=40 MinorRadius=15.5212 AngleXU=1.5708 StartAngle=5.1385 EndAngle=7.42787
    g16: LineSegment StartX=0 StartY=34.4667 StartZ=0 EndX=0 EndY=-45.5333 EndZ=0
    g17: LineSegment StartX=-15.5212 StartY=-5.53333 StartZ=0 EndX=15.5212 EndY=-5.53333 EndZ=0
    g18: GeomPoint X=4.1e-15 Y=31.3325 Z=0
    g19: GeomPoint X=0 Y=-42.3992 Z=0
    g20: LineSegment StartX=-12.9286 StartY=16.6 StartZ=0 EndX=-11.5286 EndY=16.6 EndZ=0
    g21: LineSegment StartX=-13.1295 StartY=15.8 StartZ=0 EndX=-10.7286 EndY=15.8 EndZ=0
    g22: LineSegment StartX=-11.5286 StartY=16.6 StartZ=0 EndX=-11.5286 EndY=15.8 EndZ=0
    g23: LineSegment StartX=-10.7286 StartY=15.8 StartZ=0 EndX=-10.7286 EndY=16.6 EndZ=0
    g24: LineSegment StartX=-10.7286 StartY=16.6 StartZ=0 EndX=-11.1286 EndY=17 EndZ=0
    g25: LineSegment StartX=-11.5286 StartY=16.6 StartZ=0 EndX=-10.7286 EndY=16.6 EndZ=0
    g26: LineSegment StartX=-11.5286 StartY=16.6 StartZ=0 EndX=-11.1286 EndY=17 EndZ=0
    g27: LineSegment StartX=12.9286 StartY=16.6 StartZ=0 EndX=11.5286 EndY=16.6 EndZ=0
    g28: LineSegment StartX=13.1295 StartY=15.8 StartZ=0 EndX=11.5286 EndY=15.8 EndZ=0
    g29: LineSegment StartX=11.5286 StartY=16.6 StartZ=0 EndX=11.1286 EndY=17 EndZ=0
    g30: LineSegment StartX=11.1286 StartY=17 StartZ=0 EndX=10.7286 EndY=16.6 EndZ=0
    g31: LineSegment StartX=10.7286 StartY=16.6 StartZ=0 EndX=10.7286 EndY=15.8 EndZ=0
    g32: LineSegment StartX=10.7286 StartY=15.8 StartZ=0 EndX=11.5286 EndY=15.8 EndZ=0
    g33: LineSegment StartX=11.5286 StartY=16.6 StartZ=0 EndX=11.5286 EndY=15.8 EndZ=0
    g34: LineSegment StartX=10.7286 StartY=16.6 StartZ=0 EndX=11.5286 EndY=16.6 EndZ=0
    g35: LineSegment StartX=-10.7286 StartY=16.6 StartZ=0 EndX=10.7286 EndY=16.6 EndZ=0
    g36: LineSegment StartX=-10.7286 StartY=15.8 StartZ=0 EndX=10.7286 EndY=15.8 EndZ=0
    g37: LineSegment StartX=-11.1286 StartY=17 StartZ=0 EndX=11.1286 EndY=17 EndZ=0
    g38: LineSegment StartX=-14.1333 StartY=11 StartZ=0 EndX=14.1333 EndY=11 EndZ=0
    g39: LineSegment StartX=-13.4567 StartY=14.4 StartZ=0 EndX=-13.1295 EndY=15.8 EndZ=0
    g40: LineSegment StartX=-12.9286 StartY=16.6 StartZ=0 EndX=-12.9286 EndY=13.6 EndZ=0
    g41: ArcOfEllipse CenterX=-1.42e-14 CenterY=-5.53333 CenterZ=0 NormalX=0 NormalY=0 NormalZ=1 MajorRadius=40 MinorRadius=15.5212 AngleXU=1.5708 StartAngle=5.29875 EndAngle=7.26762
    g42: LineSegment StartX=0 StartY=34.4667 StartZ=0 EndX=-2.92e-14 EndY=-45.5333 EndZ=0
    g43: LineSegment StartX=-15.5212 StartY=-5.53333 StartZ=0 EndX=15.5212 EndY=-5.53333 EndZ=0
    g44: GeomPoint X=-1.9e-15 Y=31.3325 Z=0
    g45: GeomPoint X=-2.8e-14 Y=-42.3992 Z=0
    g46: GeomPoint X=-12.9286 Y=15.1 Z=0
    g47: LineSegment StartX=-11.1286 StartY=17 StartZ=0 EndX=-11.1286 EndY=15.8 EndZ=0
    g48: LineSegment StartX=-13.4567 StartY=14.4 StartZ=0 EndX=-12.0567 EndY=14.4 EndZ=0
    g49: LineSegment StartX=-13.6304 StartY=13.6 StartZ=0 EndX=-12.0567 EndY=13.6 EndZ=0
    g50: LineSegment StartX=-12.0567 StartY=14.4 StartZ=0 EndX=-11.2567 EndY=14.4 EndZ=0
    g51: LineSegment StartX=-12.0567 StartY=13.6 StartZ=0 EndX=-11.6567 EndY=13.2 EndZ=0
    g52: LineSegment StartX=-11.6567 StartY=13.2 StartZ=0 EndX=-11.2567 EndY=13.6 EndZ=0
    g53: LineSegment StartX=-11.2567 StartY=13.6 StartZ=0 EndX=-11.2567 EndY=14.4 EndZ=0
    g54: LineSegment StartX=-12.0567 StartY=14.4 StartZ=0 EndX=-12.0567 EndY=13.6 EndZ=0
    g55: LineSegment StartX=-12.0567 StartY=13.6 StartZ=0 EndX=-11.2567 EndY=13.6 EndZ=0
    g56: LineSegment StartX=-11.6567 StartY=13.2 StartZ=0 EndX=-11.6567 EndY=14.4 EndZ=0
    g57: LineSegment StartX=-13.6304 StartY=13.6 StartZ=0 EndX=-14.1333 EndY=11 EndZ=0
    g58: LineSegment StartX=13.4567 StartY=14.4 StartZ=0 EndX=12.0567 EndY=14.4 EndZ=0
    g59: LineSegment StartX=12.0567 StartY=14.4 StartZ=0 EndX=11.2567 EndY=14.4 EndZ=0
    g60: LineSegment StartX=11.2567 StartY=14.4 StartZ=0 EndX=11.2567 EndY=13.6 EndZ=0
    g61: LineSegment StartX=11.2567 StartY=13.6 StartZ=0 EndX=11.6567 EndY=13.2 EndZ=0
    g62: LineSegment StartX=11.6567 StartY=13.2 StartZ=0 EndX=12.0567 EndY=13.6 EndZ=0
    g63: LineSegment StartX=12.0567 StartY=13.6 StartZ=0 EndX=13.6304 EndY=13.6 EndZ=0
    g64: LineSegment StartX=12.0567 StartY=13.6 StartZ=0 EndX=12.0567 EndY=14.4 EndZ=0
    g65: LineSegment StartX=11.2567 StartY=13.6 StartZ=0 EndX=12.0567 EndY=13.6 EndZ=0
    g66: LineSegment StartX=-11.2567 StartY=14.4 StartZ=0 EndX=11.2567 EndY=14.4 EndZ=0
    g67: LineSegment StartX=13.1295 StartY=15.8 StartZ=0 EndX=13.4567 EndY=14.4 EndZ=0
    g68: LineSegment StartX=13.6304 StartY=13.6 StartZ=0 EndX=14.1333 EndY=11 EndZ=0
  constraints (164):
    c: Horizontal(g0)
    c: Symmetric(g0,g0,g-1)
    c: Coincident(g1,g0)
    c: Vertical(g1)
    c: Coincident(g2,g0)
    c: Vertical(g2)
    c: Coincident(g3,g1)
    c: Coincident(g3,g2)
    c: Horizontal(g3)
    c: Coincident(g4,g2)
    c: Coincident(g5,g1)
    c: InternalAlignment(g7-g10 -> g6) x4
    c: PointOnObject(g6,g-2)
    c: Coincident(g11,g5)
    c: Coincident(g11,g4)
    c: Horizontal(g11)
    c: Coincident(g12,g1)
    c: PointOnObject(g12,g11)
    c: Vertical(g12)
    c: Coincident(g13,g2)
    c: PointOnObject(g13,g11)
    c: Vertical(g13)
    c: PointOnObject(g7,g-2)
    c: Coincident(g14,g6)
    c: Coincident(g14,g6)
    c: Coincident(g6,g5)
    c: Coincident(g6,g4)
    c: DistanceY(g0,g2) = 3.6
    c: DistanceY(g-1,g4) = 11
    c: DistanceX(g5,g4) = 30.6667
    c: DistanceX(g0,g0) = 25.5833
    c: DistanceY(g-1,g7) = 35.6667
    c: DistanceY(g8,g7) = 40
    c: InternalAlignment(g16-g19 -> g15) x4
    c: DistanceY(g17,g16) = 40
    c: Vertical(g16)
    c: PointOnObject(g16,g-2)
    c: PointOnObject(g15,g11)
    c: PointOnObject(g15,g11)
    c: DistanceX(g15,g4) = 1.2
    c: DistanceY(g16,g7) = 1.2
    c: PointOnObject(g20,g15)
    c: Horizontal(g20)
    c: PointOnObject(g21,g15)
    c: Horizontal(g21)
    c: Coincident(g22,g20)
    c: PointOnObject(g22,g21)
    c: Vertical(g22)
    c: Coincident(g23,g21)
    c: Vertical(g23)
    c: Coincident(g24,g23)
    c: Coincident(g25,g20)
    c: Coincident(g25,g23)
    c: Horizontal(g25)
    c: DistanceY(g21,g23) = 0.8
    c: Coincident(g26,g20)
    c: Coincident(g26,g24)
    c: Equal(g24,g26)
    c: Angle(g26,g24) = 1.5708
    c: PointOnObject(g27,g15)
    c: Horizontal(g27)
    c: PointOnObject(g28,g15)
    c: Horizontal(g28)
    c: Coincident(g29,g27)
    c: Coincident(g30,g29)
    c: Coincident(g31,g30)
    c: Vertical(g31)
    c: Coincident(g32,g31)
    c: Coincident(g32,g28)
    c: Coincident(g33,g27)
    c: Coincident(g33,g28)
    c: Coincident(g34,g30)
    c: Coincident(g34,g27)
    c: Horizontal(g34)
    c: Vertical(g33)
    c: Horizontal(g32)
    c: Coincident(g35,g23)
    c: Coincident(g35,g30)
    c: Horizontal(g35)
    c: Coincident(g36,g21)
    c: Coincident(g36,g31)
    c: Horizontal(g36)
    c: Angle(g30,g29) = 1.5708
    c: Coincident(g37,g24)
    c: Coincident(g37,g29)
    c: Horizontal(g37)
    c: Equal(g24,g30)
    c: DistanceX(g20,g20) = 1.4
    c: DistanceX(g27,g27) = 1.4
    c: Coincident(g38,g15)
    c: Coincident(g38,g15)
    c: PointOnObject(g39,g15)
    c: PointOnObject(g49,g15)
    c: Coincident(g39,g21)
    c: Coincident(g40,g20)
    c: Vertical(g40)
    c: InternalAlignment(g42-g45 -> g41) x4
    c: Coincident(g42,g16)
    c: Coincident(g41,g20)
    c: Coincident(g41,g27)
    c: Symmetric(g20,g40,g46)
    c: Coincident(g47,g24)
    c: PointOnObject(g47,g21)
    c: Vertical(g47)
    c: DistanceY(g21,g24) = 1.2
    c: Coincident(g48,g39)
    c: Horizontal(g48)
    c: Horizontal(g49)
    c: PointOnObject(g40,g49)
    c: Coincident(g50,g48)
    c: Horizontal(g50)
    c: Coincident(g51,g49)
    c: Coincident(g52,g51)
    c: Coincident(g53,g52)
    c: Coincident(g53,g50)
    c: Vertical(g53)
    c: Coincident(g54,g48)
    c: Coincident(g54,g49)
    c: Coincident(g55,g49)
    c: Coincident(g55,g52)
    c: Horizontal(g55)
    c: Vertical(g54)
    c: Angle(g52,g51) = 1.5708
    c: Coincident(g56,g51)
    c: PointOnObject(g56,g50)
    c: Vertical(g56)
    c: Equal(g52,g51)
    c: Equal(g52,g24)
    c: Equal(g56,g47)
    c: DistanceY(g-1,g46) = 15.1
    c: Equal(g48,g20)
    c: DistanceY(g52,g23) = 3
    c: DistanceY(g43,g16) = 40
    c: Coincident(g57,g49)
    c: Coincident(g57,g38)
    c: PointOnObject(g58,g15)
    c: Horizontal(g58)
    c: Coincident(g59,g58)
    c: Horizontal(g59)
    c: Coincident(g60,g59)
    c: Vertical(g60)
    c: Coincident(g61,g60)
    c: Coincident(g62,g61)
    c: Coincident(g63,g62)
    c: PointOnObject(g63,g15)
    c: Horizontal(g63)
    c: Coincident(g64,g62)
    c: Coincident(g64,g58)
    c: Vertical(g64)
    c: Coincident(g65,g60)
    c: Coincident(g65,g62)
    c: Horizontal(g65)
    c: Angle(g62,g61) = 1.5708
    c: Equal(g29,g62)
    c: Equal(g61,g62)
    c: Equal(g60,g31)
    c: Equal(g58,g27)
    c: Coincident(g66,g50)
    c: Coincident(g66,g59)
    c: Horizontal(g66)
    c: Coincident(g67,g28)
    c: Coincident(g67,g58)
    c: Coincident(g68,g63)
    c: Coincident(g68,g38)
FEATURE [PartDesign::SubtractiveLoft] SubtractiveLoft002  label="SubtractiveLoft_TrimClips"
  BaseFeature = -> Pad010
  Closed = false
  Placement = pos=(0,0,0) rot=(1,0,0;1.5708rad)
  Profile = -> Sketch027
  Ruled = false
  Sections = -> [Sketch028]
FEATURE [Sketcher::SketchObject] Sketch029  label="Sketch_EarClipTrimFr001"
  FullyConstrained = true
  MapMode = 5
  Placement = pos=(0,0,0) rot=(1,0,0;1.5708rad)
  Support = -> [XZ_Plane009]
  expr: Constraints[55] = <<params>>.ear_ellipse_majax
  expr: Constraints[70] = <<params>>.ear_front_tot_height / 2
  expr: Constraints[46] = <<params>>.ear_trim_thick
  expr: Constraints[40] = <<params>>.ear_ellipse_majax
  expr: Constraints[35] = <<params>>.ear_ellipse_majax
  expr: Constraints[34] = <<params>>.ear_front_tot_height
  expr: Constraints[45] = <<params>>.ear_trim_thick
  expr: Constraints[33] = <<params>>.ear_front_base_width
  expr: Constraints[32] = <<params>>.ear_front_mid_width
  expr: Constraints[31] = <<params>>.ear_front_mid_height
  expr: Constraints[30] = <<params>>.ear_base_thick + <<params>>.ear_vert_height
  expr: Constraints[72] = <<params>>.ear_front_mid_width / 2
  sketch-geometry (32):
    g0: LineSegment StartX=-13 StartY=0 StartZ=0 EndX=13 EndY=0 EndZ=0
    g1: LineSegment StartX=-13 StartY=0 StartZ=0 EndX=-13 EndY=3.6 EndZ=0
    g2: LineSegment StartX=13 StartY=0 StartZ=0 EndX=13 EndY=3.6 EndZ=0
    g3: LineSegment StartX=-13 StartY=3.6 StartZ=0 EndX=13 EndY=3.6 EndZ=0
    g4: LineSegment StartX=13 StartY=3.6 StartZ=0 EndX=16 EndY=12 EndZ=0
    g5: LineSegment StartX=-13 StartY=3.6 StartZ=0 EndX=-16 EndY=12 EndZ=0
    g6: ArcOfEllipse CenterX=0 CenterY=-2e-16 CenterZ=0 NormalX=0 NormalY=0 NormalZ=1 MajorRadius=40 MinorRadius=16.7726 AngleXU=1.5708 StartAngle=5.01708 EndAngle=7.54929
    g7: LineSegment StartX=0 StartY=40 StartZ=0 EndX=0 EndY=-40 EndZ=0
    g8: LineSegment StartX=-16.7726 StartY=-2e-16 StartZ=0 EndX=16.7726 EndY=-2e-16 EndZ=0
    g9: GeomPoint X=4e-15 Y=36.3137 Z=0
    g10: GeomPoint X=0 Y=-36.3137 Z=0
    g11: LineSegment StartX=-16 StartY=12 StartZ=0 EndX=16 EndY=12 EndZ=0
    g12: LineSegment StartX=-13 StartY=3.6 StartZ=0 EndX=-13 EndY=12 EndZ=0
    g13: LineSegment StartX=13 StartY=3.6 StartZ=0 EndX=13 EndY=12 EndZ=0
    g14: LineSegment StartX=-16 StartY=12 StartZ=0 EndX=16 EndY=12 EndZ=0
    g15: ArcOfEllipse CenterX=0 CenterY=-1.2 CenterZ=0 NormalX=0 NormalY=0 NormalZ=1 MajorRadius=40 MinorRadius=15.6783 AngleXU=1.5708 StartAngle=5.04869 EndAngle=7.51768
    g16: LineSegment StartX=0 StartY=38.8 StartZ=0 EndX=0 EndY=-41.2 EndZ=0
    g17: LineSegment StartX=-15.6783 StartY=-1.2 StartZ=0 EndX=15.6783 EndY=-1.2 EndZ=0
    g18: GeomPoint X=4.1e-15 Y=35.5993 Z=0
    g19: GeomPoint X=0 Y=-37.9993 Z=0
    g20: LineSegment StartX=-14.8 StartY=12 StartZ=0 EndX=-16 EndY=12 EndZ=0
    g21: LineSegment StartX=14.8 StartY=12 StartZ=0 EndX=16 EndY=12 EndZ=0
    g22: ArcOfEllipse CenterX=8e-16 CenterY=-6e-16 CenterZ=0 NormalX=0 NormalY=0 NormalZ=1 MajorRadius=40 MinorRadius=16.7726 AngleXU=1.5708 StartAngle=5.01708 EndAngle=7.54929
    g23: LineSegment StartX=0 StartY=40 StartZ=0 EndX=1.5e-15 EndY=-40 EndZ=0
    g24: LineSegment StartX=-16.7726 StartY=-9e-16 StartZ=0 EndX=16.7726 EndY=-3e-16 EndZ=0
    g25: GeomPoint X=4.8e-15 Y=36.3137 Z=0
    g26: GeomPoint X=1.4e-15 Y=-36.3137 Z=0
    g27: LineSegment StartX=16 StartY=12 StartZ=0 EndX=32 EndY=12 EndZ=0
    g28: LineSegment StartX=-16 StartY=12 StartZ=0 EndX=-32 EndY=12 EndZ=0
    g29: LineSegment StartX=-32 StartY=12 StartZ=0 EndX=-32 EndY=60 EndZ=0
    g30: LineSegment StartX=-32 StartY=60 StartZ=0 EndX=32 EndY=60 EndZ=0
    g31: LineSegment StartX=32 StartY=60 StartZ=0 EndX=32 EndY=12 EndZ=0
  constraints (64):
    c: Horizontal(g0)
    c: Symmetric(g0,g0,g-1)
    c: Coincident(g1,g0)
    c: Vertical(g1)
    c: Coincident(g2,g0)
    c: Vertical(g2)
    c: Coincident(g3,g1)
    c: Coincident(g3,g2)
    c: Horizontal(g3)
    c: Coincident(g4,g2)
    c: Coincident(g5,g1)
    c: InternalAlignment(g7-g10 -> g6) x4
    c: PointOnObject(g6,g-2)
    c: Coincident(g11,g5)
    c: Coincident(g11,g4)
    c: Horizontal(g11)
    c: Coincident(g12,g1)
    c: PointOnObject(g12,g11)
    c: Vertical(g12)
    c: Coincident(g13,g2)
    c: PointOnObject(g13,g11)
    c: Vertical(g13)
    c: PointOnObject(g7,g-2)
    c: Coincident(g14,g6)
    c: Coincident(g14,g6)
    c: Coincident(g6,g5)
    c: Coincident(g6,g4)
    c: DistanceY(g0,g2) = 3.6
    c: DistanceY(g-1,g4) = 12
    c: DistanceX(g5,g4) = 32
    c: DistanceX(g0,g0) = 26
    c: DistanceY(g-1,g7) = 40
    c: DistanceY(g8,g7) = 40
    c: InternalAlignment(g16-g19 -> g15) x4
    c: DistanceY(g17,g16) = 40
    c: Vertical(g16)
    c: PointOnObject(g16,g-2)
    c: PointOnObject(g15,g11)
    c: PointOnObject(g15,g11)
    c: DistanceX(g15,g4) = 1.2
    c: DistanceY(g16,g7) = 1.2
    c: Coincident(g20,g15)
    c: Coincident(g20,g5)
    c: Coincident(g21,g15)
    c: Coincident(g21,g4)
    c: InternalAlignment(g23-g26 -> g22) x4
    c: DistanceY(g22,g23) = 40
    c: Coincident(g22,g20)
    c: Coincident(g22,g21)
    c: Coincident(g23,g7)
    c: Coincident(g27,g22)
    c: Horizontal(g27)
    c: Coincident(g28,g22)
    c: Horizontal(g28)
    c: Coincident(g29,g28)
    c: Vertical(g29)
    c: Coincident(g30,g29)
    c: Horizontal(g30)
    c: Coincident(g31,g30)
    c: Coincident(g31,g27)
    c: Vertical(g31)
    c: DistanceY(g7,g30) = 20
    c: Equal(g27,g28)
    c: DistanceX(g22,g27) = 16
FEATURE [Sketcher::SketchObject] Sketch030  label="Sketch_EarClipTrimBk001"
  FullyConstrained = true
  MapMode = 5
  Placement = pos=(0,4,9e-16) rot=(1,0,0;1.5708rad)
  Support = -> [DatumPlane003]
  expr: Constraints[30] = <<params>>.ear_base_thick + <<params>>.ear_vert_height
  expr: Constraints[31] = <<params>>.ear_trim_mid_height
  expr: Constraints[32] = <<params>>.ear_trim_mid_width
  expr: Constraints[33] = <<params>>.ear_trim_base_width
  expr: Constraints[45] = <<params>>.ear_trim_thick
  expr: Constraints[71] = <<params>>.ear_front_mid_width / 2
  expr: Constraints[34] = <<params>>.ear_trim_tot_height
  expr: Constraints[35] = <<params>>.ear_ellipse_majax
  expr: Constraints[40] = <<params>>.ear_ellipse_majax
  expr: Constraints[46] = <<params>>.ear_trim_thick
  expr: Constraints[55] = <<params>>.ear_ellipse_majax
  expr: Constraints[72] = <<params>>.ear_front_tot_height / 2
  sketch-geometry (32):
    g0: LineSegment StartX=-12.7917 StartY=0 StartZ=0 EndX=12.7917 EndY=0 EndZ=0
    g1: LineSegment StartX=-12.7917 StartY=0 StartZ=0 EndX=-12.7917 EndY=3.6 EndZ=0
    g2: LineSegment StartX=12.7917 StartY=0 StartZ=0 EndX=12.7917 EndY=3.6 EndZ=0
    g3: LineSegment StartX=-12.7917 StartY=3.6 StartZ=0 EndX=12.7917 EndY=3.6 EndZ=0
    g4: LineSegment StartX=12.7917 StartY=3.6 StartZ=0 EndX=15.3333 EndY=11 EndZ=0
    g5: LineSegment StartX=-12.7917 StartY=3.6 StartZ=0 EndX=-15.3333 EndY=11 EndZ=0
    g6: ArcOfEllipse CenterX=0 CenterY=-4.33333 CenterZ=0 NormalX=0 NormalY=0 NormalZ=1 MajorRadius=40 MinorRadius=16.6015 AngleXU=1.5708 StartAngle=5.10579 EndAngle=7.46058
    g7: LineSegment StartX=0 StartY=35.6667 StartZ=0 EndX=0 EndY=-44.3333 EndZ=0
    g8: LineSegment StartX=-16.6015 StartY=-4.33333 StartZ=0 EndX=16.6015 EndY=-4.33333 EndZ=0
    g9: GeomPoint X=4e-15 Y=32.0588 Z=0
    g10: GeomPoint X=0 Y=-40.7255 Z=0
    g11: LineSegment StartX=-15.3333 StartY=11 StartZ=0 EndX=15.3333 EndY=11 EndZ=0
    g12: LineSegment StartX=-12.7917 StartY=3.6 StartZ=0 EndX=-12.7917 EndY=11 EndZ=0
    g13: LineSegment StartX=12.7917 StartY=3.6 StartZ=0 EndX=12.7917 EndY=11 EndZ=0
    g14: LineSegment StartX=-15.3333 StartY=11 StartZ=0 EndX=15.3333 EndY=11 EndZ=0
    g15: ArcOfEllipse CenterX=0 CenterY=-5.53333 CenterZ=0 NormalX=0 NormalY=0 NormalZ=1 MajorRadius=40 MinorRadius=15.5212 AngleXU=1.5708 StartAngle=5.1385 EndAngle=7.42787
    g16: LineSegment StartX=0 StartY=34.4667 StartZ=0 EndX=0 EndY=-45.5333 EndZ=0
    g17: LineSegment StartX=-15.5212 StartY=-5.53333 StartZ=0 EndX=15.5212 EndY=-5.53333 EndZ=0
    g18: GeomPoint X=4.1e-15 Y=31.3325 Z=0
    g19: GeomPoint X=0 Y=-42.3992 Z=0
    g20: LineSegment StartX=-14.1333 StartY=11 StartZ=0 EndX=-15.3333 EndY=11 EndZ=0
    g21: LineSegment StartX=14.1333 StartY=11 StartZ=0 EndX=15.3333 EndY=11 EndZ=0
    g22: ArcOfEllipse CenterX=-1.8e-15 CenterY=-4.33333 CenterZ=0 NormalX=0 NormalY=0 NormalZ=1 MajorRadius=40 MinorRadius=16.6015 AngleXU=1.5708 StartAngle=5.10579 EndAngle=7.46058
    g23: LineSegment StartX=0 StartY=35.6667 StartZ=0 EndX=-3.4e-15 EndY=-44.3333 EndZ=0
    g24: LineSegment StartX=-16.6015 StartY=-4.33333 StartZ=0 EndX=16.6015 EndY=-4.33333 EndZ=0
    g25: GeomPoint X=2.3e-15 Y=32.0588 Z=0
    g26: GeomPoint X=-3.3e-15 Y=-40.7255 Z=0
    g27: LineSegment StartX=15.3333 StartY=11 StartZ=0 EndX=31.3333 EndY=11 EndZ=0
    g28: LineSegment StartX=31.3333 StartY=11 StartZ=0 EndX=31.3333 EndY=55.6667 EndZ=0
    g29: LineSegment StartX=31.3333 StartY=55.6667 StartZ=0 EndX=-31.3333 EndY=55.6667 EndZ=0
    g30: LineSegment StartX=-31.3333 StartY=55.6667 StartZ=0 EndX=-31.3333 EndY=11 EndZ=0
    g31: LineSegment StartX=-31.3333 StartY=11 StartZ=0 EndX=-15.3333 EndY=11 EndZ=0
  constraints (64):
    c: Horizontal(g0)
    c: Symmetric(g0,g0,g-1)
    c: Coincident(g1,g0)
    c: Vertical(g1)
    c: Coincident(g2,g0)
    c: Vertical(g2)
    c: Coincident(g3,g1)
    c: Coincident(g3,g2)
    c: Horizontal(g3)
    c: Coincident(g4,g2)
    c: Coincident(g5,g1)
    c: InternalAlignment(g7-g10 -> g6) x4
    c: PointOnObject(g6,g-2)
    c: Coincident(g11,g5)
    c: Coincident(g11,g4)
    c: Horizontal(g11)
    c: Coincident(g12,g1)
    c: PointOnObject(g12,g11)
    c: Vertical(g12)
    c: Coincident(g13,g2)
    c: PointOnObject(g13,g11)
    c: Vertical(g13)
    c: PointOnObject(g7,g-2)
    c: Coincident(g14,g6)
    c: Coincident(g14,g6)
    c: Coincident(g6,g5)
    c: Coincident(g6,g4)
    c: DistanceY(g0,g2) = 3.6
    c: DistanceY(g-1,g4) = 11
    c: DistanceX(g5,g4) = 30.6667
    c: DistanceX(g0,g0) = 25.5833
    c: DistanceY(g-1,g7) = 35.6667
    c: DistanceY(g8,g7) = 40
    c: InternalAlignment(g16-g19 -> g15) x4
    c: DistanceY(g17,g16) = 40
    c: Vertical(g16)
    c: PointOnObject(g16,g-2)
    c: PointOnObject(g15,g11)
    c: PointOnObject(g15,g11)
    c: DistanceX(g15,g4) = 1.2
    c: DistanceY(g16,g7) = 1.2
    c: Coincident(g20,g15)
    c: Coincident(g20,g5)
    c: Coincident(g21,g15)
    c: Coincident(g21,g4)
    c: InternalAlignment(g23-g26 -> g22) x4
    c: DistanceY(g22,g23) = 40
    c: Coincident(g22,g20)
    c: Coincident(g22,g21)
    c: Coincident(g23,g7)
    c: Coincident(g27,g22)
    c: Horizontal(g27)
    c: Coincident(g28,g27)
    c: Vertical(g28)
    c: Coincident(g29,g28)
    c: Horizontal(g29)
    c: Coincident(g30,g29)
    c: Vertical(g30)
    c: Coincident(g31,g30)
    c: Coincident(g31,g22)
    c: Horizontal(g31)
    c: Equal(g27,g31)
    c: DistanceX(g22,g27) = 16
    c: DistanceY(g7,g28) = 20
FEATURE [PartDesign::SubtractiveLoft] SubtractiveLoft003
  BaseFeature = -> SubtractiveLoft002
  Closed = false
  Placement = pos=(0,0,0) rot=(1,0,0;1.5708rad)
  Profile = -> Sketch029
  Ruled = false
  Sections = -> [Sketch030]
FEATURE [PartDesign::Body] Body008  label="EarTrim"
  Group = -> [Sketch020,DatumPlane003,Sketch021,AdditiveLoft001,Sketch025,Pad009,Sketch026,Pad010,Sketch027,Sketch028,SubtractiveLoft002,Sketch029,Sketch030,SubtractiveLoft003]
  Origin = -> Origin010
  Tip = -> SubtractiveLoft003
FEATURE [Sketcher::SketchObject] Sketch031
  FullyConstrained = true
  MapMode = 5
  Support = -> [XY_Plane020]
  expr: Constraints[10] = <<std_params>>.pin_square_block_dim
  expr: Constraints[11] = <<std_params>>.pin_square_block_dim * 3
  expr: Constraints[12] = <<std_params>>.mic_pin_offset_width
  sketch-geometry (5):
    g0: LineSegment StartX=-3.81 StartY=12.88 StartZ=0 EndX=3.81 EndY=12.88 EndZ=0
    g1: LineSegment StartX=3.81 StartY=12.88 StartZ=0 EndX=3.81 EndY=10.34 EndZ=0
    g2: LineSegment StartX=3.81 StartY=10.34 StartZ=0 EndX=-3.81 EndY=10.34 EndZ=0
    g3: LineSegment StartX=-3.81 StartY=10.34 StartZ=0 EndX=-3.81 EndY=12.88 EndZ=0
    g4: GeomPoint X=0 Y=11.61 Z=0
  constraints (13):
    c: Coincident(g0,g1)
    c: Coincident(g1,g2)
    c: Coincident(g2,g3)
    c: Coincident(g3,g0)
    c: Horizontal(g0)
    c: Horizontal(g2)
    c: Vertical(g1)
    c: Vertical(g3)
    c: Symmetric(g2,g0,g4)
    c: PointOnObject(g4,g-2)
    c: DistanceY(g1,g1) = 2.54
    c: DistanceX(g0,g0) = 7.62
    c: DistanceY(g-1,g4) = 11.61
FEATURE [Sketcher::SketchObject] Sketch032
  FullyConstrained = true
  MapMode = 5
  Support = -> [XY_Plane022]
  expr: Constraints[17] = 2.54 / 4
  sketch-geometry (9):
    g0: LineSegment StartX=-0.865 StartY=5.27 StartZ=0 EndX=0.865 EndY=5.27 EndZ=0
    g1: LineSegment StartX=1.5 StartY=4.635 StartZ=0 EndX=1.5 EndY=1.905 EndZ=0
    g2: LineSegment StartX=0.865 StartY=1.27 StartZ=0 EndX=-0.865 EndY=1.27 EndZ=0
    g3: LineSegment StartX=-1.5 StartY=1.905 StartZ=0 EndX=-1.5 EndY=4.635 EndZ=0
    g4: ArcOfCircle CenterX=0.865 CenterY=4.635 CenterZ=0 NormalX=0 NormalY=0 NormalZ=1 AngleXU=0 Radius=0.635 StartAngle=-9e-16 EndAngle=1.5708
    g5: ArcOfCircle CenterX=0.865 CenterY=1.905 CenterZ=0 NormalX=0 NormalY=0 NormalZ=1 AngleXU=0 Radius=0.635 StartAngle=4.71239 EndAngle=6.28319
    g6: ArcOfCircle CenterX=-0.865 CenterY=1.905 CenterZ=0 NormalX=0 NormalY=0 NormalZ=1 AngleXU=0 Radius=0.635 StartAngle=3.14159 EndAngle=4.71239
    g7: ArcOfCircle CenterX=-0.865 CenterY=4.635 CenterZ=0 NormalX=0 NormalY=0 NormalZ=1 AngleXU=0 Radius=0.635 StartAngle=1.5708 EndAngle=3.14159
    g8: GeomPoint X=0 Y=3.27 Z=0
  constraints (21):
    c: Horizontal(g0)
    c: Horizontal(g2)
    c: Vertical(g1)
    c: Vertical(g3)
    c: Tangent(g1,g4) = 1.5708
    c: Tangent(g0,g4) = 1.5708
    c: Tangent(g1,g5) = 1.5708
    c: Tangent(g2,g5) = 1.5708
    c: Tangent(g2,g6) = 1.5708
    c: Tangent(g3,g6) = 1.5708
    c: Tangent(g3,g7) = 1.5708
    c: Tangent(g0,g7) = 1.5708
    c: Equal(g7,g4)
    c: Equal(g4,g5)
    c: Equal(g5,g6)
    c: PointOnObject(g8,g-2)
    c: Symmetric(g6,g4,g8)
    c: Radius(g4) = 0.635
    c: DistanceY(g2,g0) = 4
    c: DistanceX(g3,g1) = 3
    c: DistanceY(g-1,g2) = 1.27
FEATURE [Sketcher::SketchObject] Sketch033
  FullyConstrained = true
  MapMode = 5
  Support = -> [XY_Plane017]
  expr: Constraints[12] = <<std_params>>.pin_square_block_dim * 3 - 2 * <<std_params>>.std_tol
  expr: Constraints[11] = <<std_params>>.pin_width
  expr: Constraints[10] = <<std_params>>.light_width / 2 - <<std_params>>.light_hole_edge_offset
  sketch-geometry (5):
    g0: LineSegment StartX=-3.51 StartY=-5.415 StartZ=0 EndX=3.51 EndY=-5.415 EndZ=0
    g1: LineSegment StartX=3.51 StartY=-5.415 StartZ=0 EndX=3.51 EndY=-6.015 EndZ=0
    g2: LineSegment StartX=3.51 StartY=-6.015 StartZ=0 EndX=-3.51 EndY=-6.015 EndZ=0
    g3: LineSegment StartX=-3.51 StartY=-6.015 StartZ=0 EndX=-3.51 EndY=-5.415 EndZ=0
    g4: GeomPoint X=0 Y=-5.715 Z=0
  constraints (13):
    c: Coincident(g0,g1)
    c: Coincident(g1,g2)
    c: Coincident(g2,g3)
    c: Coincident(g3,g0)
    c: Horizontal(g0)
    c: Horizontal(g2)
    c: Vertical(g1)
    c: Vertical(g3)
    c: PointOnObject(g4,g-2)
    c: Symmetric(g2,g0,g4)
    c: DistanceY(g4,g-1) = 5.715
    c: DistanceY(g1,g1) = 0.6
    c: DistanceX(g2,g2) = 7.02
FEATURE [Sketcher::SketchObject] Sketch034
  FullyConstrained = true
  MapMode = 5
  Placement = pos=(0,0,0) rot=(1,0,0;1.5708rad)
  Support = -> [XZ_Plane017]
  expr: Constraints[57] = <<std_params>>.pin_leng * 2
  expr: Constraints[58] = <<std_params>>.pin_square_block_dim - <<std_params>>.std_tol
  expr: Constraints[59] = <<std_params>>.pin_width
  expr: Constraints[61] = <<std_params>>.pin_spacing
  sketch-geometry (24):
    g0: LineSegment StartX=-2.24 StartY=14.64 StartZ=0 EndX=-0.3 EndY=14.64 EndZ=0
    g1: LineSegment StartX=-0.3 StartY=14.64 StartZ=0 EndX=-0.3 EndY=2.24 EndZ=0
    g2: LineSegment StartX=-0.3 StartY=2.24 StartZ=0 EndX=-2.24 EndY=2.24 EndZ=0
    g3: LineSegment StartX=-2.24 StartY=2.24 StartZ=0 EndX=-2.24 EndY=14.64 EndZ=0
    g4: LineSegment StartX=0.3 StartY=14.64 StartZ=0 EndX=2.24 EndY=14.64 EndZ=0
    g5: LineSegment StartX=2.24 StartY=14.64 StartZ=0 EndX=2.24 EndY=2.24 EndZ=0
    g6: LineSegment StartX=2.24 StartY=2.24 StartZ=0 EndX=0.3 EndY=2.24 EndZ=0
    g7: LineSegment StartX=0.3 StartY=2.24 StartZ=0 EndX=0.3 EndY=14.64 EndZ=0
    g8: LineSegment StartX=2.84 StartY=14.64 StartZ=0 EndX=4.78 EndY=14.64 EndZ=0
    g9: LineSegment StartX=4.78 StartY=14.64 StartZ=0 EndX=4.78 EndY=2.24 EndZ=0
    g10: LineSegment StartX=4.78 StartY=2.24 StartZ=0 EndX=2.84 EndY=2.24 EndZ=0
    g11: LineSegment StartX=2.84 StartY=2.24 StartZ=0 EndX=2.84 EndY=14.64 EndZ=0
    g12: LineSegment StartX=-4.78 StartY=14.64 StartZ=0 EndX=-2.84 EndY=14.64 EndZ=0
    g13: LineSegment StartX=-2.84 StartY=14.64 StartZ=0 EndX=-2.84 EndY=2.24 EndZ=0
    g14: LineSegment StartX=-2.84 StartY=2.24 StartZ=0 EndX=-4.78 EndY=2.24 EndZ=0
    g15: LineSegment StartX=-4.78 StartY=2.24 StartZ=0 EndX=-4.78 EndY=14.64 EndZ=0
    g16: LineSegment StartX=-2.84 StartY=14.64 StartZ=0 EndX=-2.24 EndY=14.64 EndZ=0
    g17: LineSegment StartX=-0.3 StartY=14.64 StartZ=0 EndX=0.3 EndY=14.64 EndZ=0
    g18: LineSegment StartX=2.24 StartY=14.64 StartZ=0 EndX=2.84 EndY=14.64 EndZ=0
    g19: LineSegment StartX=-2.84 StartY=2.24 StartZ=0 EndX=-2.24 EndY=2.24 EndZ=0
    g20: LineSegment StartX=-0.3 StartY=2.24 StartZ=0 EndX=0.3 EndY=2.24 EndZ=0
    g21: LineSegment StartX=2.24 StartY=2.24 StartZ=0 EndX=2.84 EndY=2.24 EndZ=0
    g22: GeomPoint X=0 Y=2.24 Z=0
    g23: GeomPoint X=2.54 Y=2.24 Z=0
  constraints (62):
    c: Coincident(g0,g1)
    c: Coincident(g1,g2)
    c: Coincident(g2,g3)
    c: Coincident(g3,g0)
    c: Horizontal(g0)
    c: Horizontal(g2)
    c: Vertical(g1)
    c: Vertical(g3)
    c: Coincident(g4,g5)
    c: Coincident(g5,g6)
    c: Coincident(g6,g7)
    c: Coincident(g7,g4)
    c: Horizontal(g4)
    c: Horizontal(g6)
    c: Vertical(g5)
    c: Vertical(g7)
    c: Coincident(g8,g9)
    c: Coincident(g9,g10)
    c: Coincident(g10,g11)
    c: Coincident(g11,g8)
    c: Horizontal(g8)
    c: Horizontal(g10)
    c: Vertical(g9)
    c: Vertical(g11)
    c: Coincident(g12,g13)
    c: Coincident(g13,g14)
    c: Coincident(g14,g15)
    c: Coincident(g15,g12)
    c: Horizontal(g12)
    c: Horizontal(g14)
    c: Vertical(g13)
    c: Vertical(g15)
    c: Equal(g12,g0)
    c: Equal(g0,g4)
    c: Equal(g4,g8)
    c: Coincident(g16,g12)
    c: Coincident(g16,g0)
    c: Coincident(g17,g0)
    c: Coincident(g17,g4)
    c: Horizontal(g17)
    c: Coincident(g18,g4)
    c: Coincident(g18,g8)
    c: Horizontal(g18)
    c: Coincident(g19,g13)
    c: Coincident(g19,g2)
    c: Coincident(g20,g1)
    c: Coincident(g20,g6)
    c: Coincident(g21,g5)
    c: Coincident(g21,g10)
    c: Equal(g16,g17)
    c: Equal(g17,g18)
    c: Horizontal(g16)
    c: Horizontal(g19)
    c: Horizontal(g20)
    c: Horizontal(g21)
    c: PointOnObject(g22,g-2)
    c: Symmetric(g1,g6,g22)
    c: DistanceY(g9,g9) = 12.4
    c: DistanceY(g-1,g22) = 2.24
    c: DistanceX(g17,g17) = 0.6
    c: Symmetric(g5,g10,g23)
    c: DistanceX(g22,g23) = 2.54
FEATURE [Sketcher::SketchObject] Sketch035
  FullyConstrained = true
  MapMode = 5
  Support = -> [XY_Plane018]
  expr: Constraints[12] = <<std_params>>.mic_pin_offset_width
  expr: Constraints[11] = <<std_params>>.pin_square_block_dim * 3
  expr: Constraints[10] = <<std_params>>.pin_square_block_dim
  sketch-geometry (5):
    g0: LineSegment StartX=-3.81 StartY=12.88 StartZ=0 EndX=3.81 EndY=12.88 EndZ=0
    g1: LineSegment StartX=3.81 StartY=12.88 StartZ=0 EndX=3.81 EndY=10.34 EndZ=0
    g2: LineSegment StartX=3.81 StartY=10.34 StartZ=0 EndX=-3.81 EndY=10.34 EndZ=0
    g3: LineSegment StartX=-3.81 StartY=10.34 StartZ=0 EndX=-3.81 EndY=12.88 EndZ=0
    g4: GeomPoint X=0 Y=11.61 Z=0
  constraints (13):
    c: Coincident(g0,g1)
    c: Coincident(g1,g2)
    c: Coincident(g2,g3)
    c: Coincident(g3,g0)
    c: Horizontal(g0)
    c: Horizontal(g2)
    c: Vertical(g1)
    c: Vertical(g3)
    c: Symmetric(g2,g0,g4)
    c: PointOnObject(g4,g-2)
    c: DistanceY(g1,g1) = 2.54
    c: DistanceX(g0,g0) = 7.62
    c: DistanceY(g-1,g4) = 11.61
FEATURE [Sketcher::SketchObject] Sketch036
  FullyConstrained = true
  MapMode = 5
  Support = -> [XY_Plane021]
  expr: Constraints[16] = <<std_params>>.mic_hole_diam
  expr: Constraints[17] = <<std_params>>.mic_leng
  expr: Constraints[18] = <<std_params>>.mic_width
  sketch-geometry (8):
    g0: LineSegment StartX=-6.75 StartY=12.5 StartZ=0 EndX=6.75 EndY=12.5 EndZ=0
    g1: LineSegment StartX=9 StartY=10.25 StartZ=0 EndX=9 EndY=2.25 EndZ=0
    g2: LineSegment StartX=6.75 StartY=0 StartZ=0 EndX=-6.75 EndY=0 EndZ=0
    g3: LineSegment StartX=-9 StartY=2.25 StartZ=0 EndX=-9 EndY=10.25 EndZ=0
    g4: ArcOfCircle CenterX=6.75 CenterY=2.25 CenterZ=0 NormalX=0 NormalY=0 NormalZ=1 AngleXU=0 Radius=2.25 StartAngle=4.71239 EndAngle=6.28319
    g5: ArcOfCircle CenterX=6.75 CenterY=10.25 CenterZ=0 NormalX=0 NormalY=0 NormalZ=1 AngleXU=0 Radius=2.25 StartAngle=1e-16 EndAngle=1.5708
    g6: ArcOfCircle CenterX=-6.75 CenterY=10.25 CenterZ=0 NormalX=0 NormalY=0 NormalZ=1 AngleXU=0 Radius=2.25 StartAngle=1.5708 EndAngle=3.14159
    g7: ArcOfCircle CenterX=-6.75 CenterY=2.25 CenterZ=0 NormalX=0 NormalY=0 NormalZ=1 AngleXU=0 Radius=2.25 StartAngle=3.14159 EndAngle=4.71239
  constraints (19):
    c: Horizontal(g0)
    c: Horizontal(g2)
    c: Vertical(g1)
    c: Vertical(g3)
    c: Tangent(g2,g4) = 1.5708
    c: Tangent(g1,g4) = 1.5708
    c: Tangent(g1,g5) = 1.5708
    c: Tangent(g0,g5) = 1.5708
    c: Tangent(g0,g6) = 1.5708
    c: Tangent(g3,g6) = 1.5708
    c: Tangent(g3,g7) = 1.5708
    c: Tangent(g2,g7) = 1.5708
    c: Equal(g6,g5)
    c: Equal(g5,g4)
    c: Equal(g4,g7)
    c: Symmetric(g2,g2,g-1)
    c: Radius(g4) = 2.25
    c: DistanceX(g3,g1) = 18
    c: DistanceY(g2,g0) = 12.5
FEATURE [Sketcher::SketchObject] Sketch037
  FullyConstrained = true
  MapMode = 5
  Support = -> [XY_Plane021]
  expr: Constraints[6] = <<std_params>>.mic_hole_offset_width
  expr: Constraints[7] = <<std_params>>.mic_hole_space_leng
  expr: Constraints[8] = <<std_params>>.mic_hole_diam
  sketch-geometry (4):
    g0: Circle CenterX=-6.5 CenterY=10.2 CenterZ=0 NormalX=0 NormalY=0 NormalZ=1 AngleXU=0 Radius=1.125
    g1: Circle CenterX=6.5 CenterY=10.2 CenterZ=0 NormalX=0 NormalY=0 NormalZ=1 AngleXU=0 Radius=1.125
    g2: LineSegment StartX=-6.5 StartY=10.2 StartZ=0 EndX=6.5 EndY=10.2 EndZ=0
    g3: GeomPoint X=0 Y=10.2 Z=0
  constraints (9):
    c: Coincident(g2,g0)
    c: Coincident(g2,g1)
    c: Horizontal(g2)
    c: PointOnObject(g3,g-2)
    c: Symmetric(g0,g1,g3)
    c: Equal(g0,g1)
    c: DistanceY(g-1,g3) = 10.2
    c: DistanceX(g2,g2) = 13
    c: Diameter(g1) = 2.25
FEATURE [Sketcher::SketchObject] Sketch038
  FullyConstrained = true
  MapMode = 5
  Support = -> [XY_Plane021]
  expr: Constraints[10] = <<std_params>>.mic_pin_offset_width
  expr: Constraints[11] = <<std_params>>.pin_hole_diam
  expr: Constraints[12] = <<std_params>>.pin_spacing
  sketch-geometry (5):
    g0: Circle CenterX=0 CenterY=11.61 CenterZ=0 NormalX=0 NormalY=0 NormalZ=1 AngleXU=0 Radius=0.4
    g1: Circle CenterX=2.54 CenterY=11.61 CenterZ=0 NormalX=0 NormalY=0 NormalZ=1 AngleXU=0 Radius=0.4
    g2: Circle CenterX=-2.54 CenterY=11.61 CenterZ=0 NormalX=0 NormalY=0 NormalZ=1 AngleXU=0 Radius=0.4
    g3: LineSegment StartX=-2.54 StartY=11.61 StartZ=0 EndX=0 EndY=11.61 EndZ=0
    g4: LineSegment StartX=0 StartY=11.61 StartZ=0 EndX=2.54 EndY=11.61 EndZ=0
  constraints (13):
    c: PointOnObject(g0,g-2)
    c: Coincident(g3,g2)
    c: Coincident(g3,g0)
    c: Coincident(g4,g0)
    c: Coincident(g4,g1)
    c: Horizontal(g3)
    c: Horizontal(g4)
    c: Equal(g2,g0)
    c: Equal(g0,g1)
    c: Equal(g3,g4)
    c: DistanceY(g-1,g0) = 11.61
    c: Diameter(g1) = 0.8
    c: DistanceX(g3,g3) = 2.54
FEATURE [Spreadsheet::Sheet] Spreadsheet001  label="std_params"
  cells = A1=Inch to mm; B1(intomm)==25.4mm; E1=std tol; F1(std_tol)==0.3mm; A3=Adafruit I2C Exp; E3=Adafruit Temp I2C; I3=Adafruit Light; B4=Inch; C4=mm; F4=Inch; G4=mm; J4=Inch; K4=mm; A5=Length; B5=1.2; C5(exp_i2c_leng)==B5 * B$1; E5=Length; F5=0.8; G5(temp_leng)==F5 * $B$1; I5=Length; J5=0.65; K5(light_leng)==J5 * $B$1; A6=Width; B6=0.7; C6(exp_i2c_width)==B6 * B$1; E6=Width; F6=0.5; G6(temp_width)==F6 * $B$1; I6=Width; J6=0.65; K6(light_width)==J6 * $B$1; A7=Hole Leng Space; B7=1; C7(exp_i2c_hole_leng_space)==B7 * B$1; E7=Hole Leng Space; F7=0.6; G7(temp_hole_leng_space)==F7 * $B$1; I7=Hole Leng Space; J7=0.45; K7(light_hole_leng_space)==J7 * $B$1; A8=Hole Diam; B8=0.1; C8(exp_i2c_hole_mt_diam)==B8 * B$1; E8=Hole Diam; F8=0.1; G8(temp_hole_diam)==F8 * $B$1; I8=Hole Diam; J8=0.1; K8(light_hole_diam)==J8 * $B$1; A9=Num Pins; B9(exp_i2c_num_pins)=12; E9=Hole Edge Offset; F9=0.1; G9(temp_hole_edge_offset)==F9 * $B$1; I9=Hole Edge Offset; J9=0.1; K9(light_hole_edge_offset)==J9 * $B$1; A10=Pin Width Space; B10=0.6; C10(exp_i2c_pin_width_space)==B10 * B$1; E10=Pin Edge Offset; F10=0.09; G10(temp_pin_edge_offset)==F10 * $B$1; I10=Pin Edge Offset; J10=0.1; K10(light_pin_edge_offset)==J10 * $B$1; E11=Num Pins; F11(temp_num_pins)=8; I11=Num Pins; J11(light_num_pins)=5; A12=General Parameters; A13=Board Thick; B13(board_thickness)==1.65mm; E13=DF Robot Fermion MEMS Mic; E14=Length; F14(mic_leng)==18mm; A15=Pin Hole Diam; B15(pin_hole_diam)==0.8mm; E15=Width; F15(mic_width)==12.5mm; A16=Pin Hole Space; B16(pin_hole_space)==2.54mm; E16=Hole Space Leng; F16(mic_hole_space_leng)==13mm; A17=Pin Width; B17(pin_width)==0.6mm; E17=Hole Offset Width; F17(mic_hole_offset_width)==10.2mm; A18=Pin Square Block Dim; B18(pin_square_block_dim)==2.54mm; E18=Pin Offset Width; F18(mic_pin_offset_width)==10.2mm + 1.41mm; A19=Pin Leng; B19(pin_leng)==6.2mm; E19=Hole Diam; F19(mic_hole_diam)==2.25mm; A20=Pin Jumper Leng; B20(pin_jumper_leng)==14.1mm; A21=Pin Spacing; B21(pin_spacing)==2.54mm
FEATURE [PartDesign::Pad] Pad001
  Direction = (1,1,1)
  Length = 1
  Length2 = 100
  Profile = -> Sketch032
  Type = 0
FEATURE [PartDesign::Fillet] Fillet001
  Base = -> Pad001 [Edge4]
  BaseFeature = -> Pad001
  Radius = 0.6
  SupportTransform = false
FEATURE [PartDesign::Body] Body009  label="Mic"
  Group = -> [Sketch032,Pad001,Fillet001]
  Origin = -> Origin019
  Tip = -> Fillet001
FEATURE [PartDesign::Pad] Pad011
  Direction = (1,1,1)
  Length = 8.74
  Length2 = 100
  Profile = -> Sketch033
  Type = 0
  expr: Length = <<std_params>>.pin_square_block_dim + <<std_params>>.pin_leng
FEATURE [PartDesign::Pocket] Pocket012
  BaseFeature = -> Pad011
  Length = 5
  Length2 = 100
  Midplane = true
  Profile = -> Sketch034
  Type = 1
FEATURE [PartDesign::Body] Body013  label="Pins002"
  Group = -> [Sketch033,Pad011,Sketch034,Pocket012]
  Origin = -> Origin017
  Placement = pos=(0,5.9,-1.7) rot=(1,0,0;3.14159rad)
  Tip = -> Pocket012
FEATURE [PartDesign::Pad] Pad012
  Direction = (1,1,1)
  Length = 1.65
  Length2 = 100
  Profile = -> Sketch036
  Reversed = true
  Type = 0
  expr: Length = <<std_params>>.board_thickness
FEATURE [PartDesign::Pocket] Pocket011
  BaseFeature = -> Pad012
  Length = 5
  Length2 = 100
  Profile = -> Sketch037
  Type = 1
FEATURE [PartDesign::Pocket] Pocket001
  BaseFeature = -> Pocket011
  Length = 5
  Length2 = 100
  Profile = -> Sketch038
  Type = 1
FEATURE [PartDesign::Body] Body003  label="MainBoard003"
  Group = -> [Sketch036,Pad012,Sketch037,Pocket011,Sketch038,Pocket001]
  Origin = -> Origin021
  Tip = -> Pocket001
FEATURE [PartDesign::Pad] Pad013
  Direction = (1,1,1)
  Length = 14.1
  Length2 = 100
  Profile = -> Sketch035
  Reversed = true
  Type = 0
  expr: Length = <<std_params>>.pin_jumper_leng
FEATURE [PartDesign::Body] Body014  label="JumperHeader"
  Group = -> [Sketch035,Pad013]
  Origin = -> Origin018
  Placement = pos=(0,0,-4.2) rot=(0,0,1;0rad)
  Tip = -> Pad013
FEATURE [PartDesign::Pad] Pad002
  Direction = (1,1,1)
  Length = 2.54
  Length2 = 100
  Profile = -> Sketch031
  Reversed = true
  Type = 0
  expr: Length = <<std_params>>.pin_square_block_dim
FEATURE [PartDesign::Body] Body004  label="PinBlock"
  Group = -> [Sketch031,Pad002]
  Origin = -> Origin020
  Placement = pos=(0,0,-1.6) rot=(0,0,1;0rad)
  Tip = -> Pad002
FEATURE [App::Part] Part003  label="DFR_AnalogMic_Part"
  Group = -> [Body003,Body009,Body004,Body013,Body014]
  Origin = -> Origin003
  Placement = pos=(2e-15,5.3,16.2) rot=(0,-0.707107,0.707107;3.14159rad)
FEATURE [Sketcher::SketchObject] Sketch039
  FullyConstrained = true
  MapMode = 5
  Placement = pos=(0,0,0) rot=(1,0,0;1.5708rad)
  Support = -> [XZ_Plane001]
  expr: Constraints[10] = <<params>>.mic_pins_square_block_dim + <<params>>.std_clear_tol
  expr: Constraints[11] = <<params>>.mic_pins_width + <<params>>.std_clear_tol
  expr: Constraints[12] = <<params>>.mic_pins_base_offset
  expr: Constraints[18] = <<params>>.std_rad
  sketch-geometry (8):
    g0: LineSegment StartX=-3.96 StartY=6.01 StartZ=0 EndX=3.96 EndY=6.01 EndZ=0
    g1: LineSegment StartX=3.96 StartY=6.01 StartZ=0 EndX=3.96 EndY=3.17 EndZ=0
    g2: LineSegment StartX=3.96 StartY=3.17 StartZ=0 EndX=-3.96 EndY=3.17 EndZ=0
    g3: LineSegment StartX=-3.96 StartY=3.17 StartZ=0 EndX=-3.96 EndY=6.01 EndZ=0
    g4: GeomPoint X=0 Y=4.59 Z=0
    g5: LineSegment StartX=-3.96 StartY=6.01 StartZ=0 EndX=-1.28558 EndY=8.25411 EndZ=0
    g6: LineSegment StartX=3.96 StartY=6.01 StartZ=0 EndX=1.28558 EndY=8.25411 EndZ=0
    g7: ArcOfCircle CenterX=0 CenterY=6.72202 CenterZ=0 NormalX=0 NormalY=0 NormalZ=1 AngleXU=0 Radius=2 StartAngle=0.872665 EndAngle=2.26893
  constraints (20):
    c: Coincident(g0,g1)
    c: Coincident(g1,g2)
    c: Coincident(g2,g3)
    c: Coincident(g3,g0)
    c: Horizontal(g0)
    c: Horizontal(g2)
    c: Vertical(g1)
    c: Vertical(g3)
    c: PointOnObject(g4,g-2)
    c: Symmetric(g2,g0,g4)
    c: DistanceY(g1,g1) = 2.84
    c: DistanceX(g0,g0) = 7.92
    c: DistanceY(g-1,g4) = 4.59
    c: Coincident(g5,g3)
    c: Coincident(g6,g1)
    c: Tangent(g5,g7) = 1.5708
    c: Tangent(g6,g7) = -1.5708
    c: Angle(g5,g6) = 1.74533
    c: Radius(g7) = 2
    c: PointOnObject(g7,g-2)
FEATURE [PartDesign::Pocket] Pocket013  label="Pocket_PinSlot"
  BaseFeature = -> Pocket010
  Length = 5
  Length2 = 100
  Placement = pos=(0,0,0) rot=(1,0,0;1.5708rad)
  Profile = -> Sketch039
  Type = 1
FEATURE [PartDesign::Body] Body  label="EarMt"
  Group = -> [DatumPlane,Sketch,Sketch001,AdditiveLoft,Sketch002,Pocket,Sketch003,Sketch004,DatumPlane001,Sketch015,Sketch016,Sketch017,SubtractiveLoft,Sketch018,Pocket008,DatumPlane002,Sketch019,Pocket009,DatumPlane004,Sketch022,Sketch023,SubtractiveLoft001,Sketch024,Pocket010,Sketch039,Pocket013]
  Origin = -> Origin001
  Tip = -> Pocket013
FEATURE [App::Part] Part  label="Part_EarMt"
  Group = -> [Body,Body008]
  Origin = -> Origin
FEATURE [Mesh::Feature] Mesh  label="EarMt (Meshed)"
